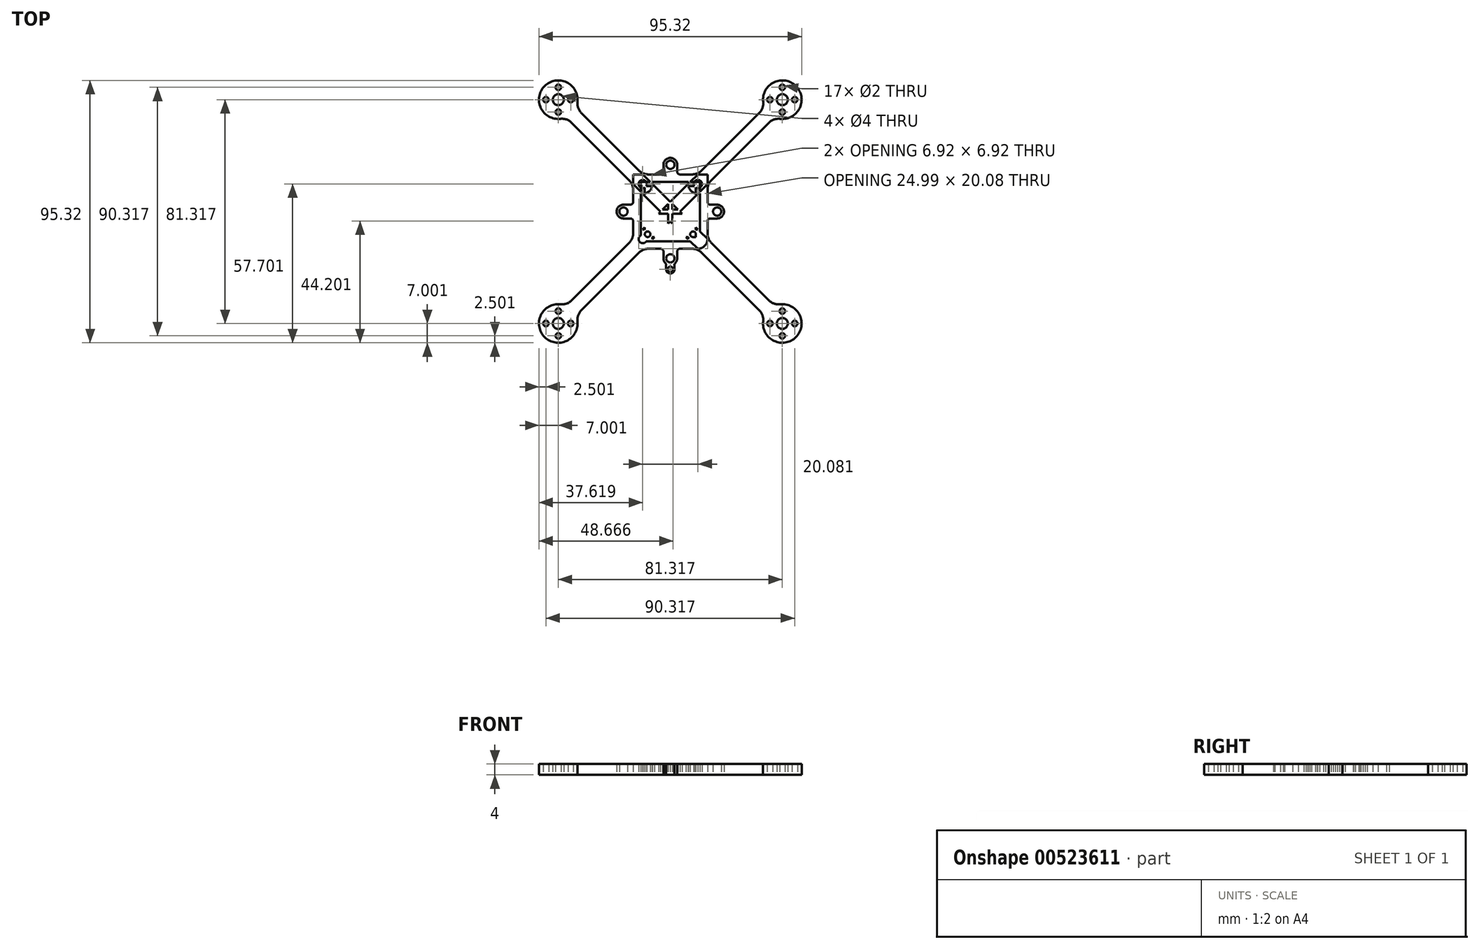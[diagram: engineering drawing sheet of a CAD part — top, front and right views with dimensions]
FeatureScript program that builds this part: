
annotation { "Feature Type Name" : "Feature", "Feature Type Description" : "" }
export const myFeature = defineFeature(function(context is Context, id is Id, definition is map)
    precondition{}
    {
        {
            var Q0;
            Q0=qCreatedBy(makeId("Top.planeOp"),FACE);
            var sketch = newSketch(context, id + "F0", { "sketchPlane" : qUnion([Q0])});
            skLineSegment(sketch, "E0", {"start": v(-40.66, 40.66) * mm, "end": v(40.66, -40.66) * mm});
            skLineSegment(sketch, "E1", {"start": v(40.66, 40.66) * mm, "end": v(-40.66, -40.66) * mm});
            skLineSegment(sketch, "E2.bottom", {"start": v(-13.5, 13.5) * mm, "end": v(13.5, 13.5) * mm});
            skLineSegment(sketch, "E2.top", {"start": v(-13.5, -13.5) * mm, "end": v(13.5, -13.5) * mm});
            skLineSegment(sketch, "E2.left", {"start": v(-13.5, 13.5) * mm, "end": v(-13.5, -13.5) * mm});
            skLineSegment(sketch, "E2.right", {"start": v(13.5, 13.5) * mm, "end": v(13.5, -13.5) * mm});
            skPoint(sketch, "E2.middle", {"position": v(0, 0) * mm});
            skCircle(sketch, "E3", {"center": v(-40.66, 40.66) * mm, "radius": 7 * mm});
            skCircle(sketch, "E4", {"center": v(-40.66, -40.66) * mm, "radius": 7 * mm});
            skCircle(sketch, "E5", {"center": v(40.66, -40.66) * mm, "radius": 7 * mm});
            skCircle(sketch, "E6", {"center": v(40.66, 40.66) * mm, "radius": 7 * mm});
            skPoint(sketch, "E7", {"position": v(-10, 10) * mm});
            skPoint(sketch, "E8", {"position": v(10, 10) * mm});
            skPoint(sketch, "E9", {"position": v(10, -10) * mm});
            skPoint(sketch, "E10", {"position": v(-10, -10) * mm});
            skCircle(sketch, "E11", {"center": v(0, 17) * mm, "radius": 1.5 * mm});
            skCircle(sketch, "E12", {"center": v(-17, 0) * mm, "radius": 1.5 * mm});
            skCircle(sketch, "E13", {"center": v(0, -17) * mm, "radius": 1.5 * mm});
            skCircle(sketch, "E14", {"center": v(0, -21) * mm, "radius": 1 * mm});
            skCircle(sketch, "E15", {"center": v(17, 0) * mm, "radius": 1.5 * mm});
            skCircle(sketch, "E16", {"center": v(0, 17) * mm, "radius": 2.5 * mm});
            skCircle(sketch, "E17", {"center": v(-17, 0) * mm, "radius": 2.5 * mm});
            skCircle(sketch, "E18", {"center": v(0, -17) * mm, "radius": 2.5 * mm});
            skCircle(sketch, "E19", {"center": v(17, 0) * mm, "radius": 2.5 * mm});
            skLineSegment(sketch, "E20", {"start": v(-2.5, 17) * mm, "end": v(-2.5, 13.5) * mm});
            skLineSegment(sketch, "E21", {"start": v(2.5, 17) * mm, "end": v(2.5, 13.5) * mm});
            skLineSegment(sketch, "E22", {"start": v(17, 2.5) * mm, "end": v(13.5, 2.5) * mm});
            skLineSegment(sketch, "E23", {"start": v(17, -2.5) * mm, "end": v(13.5, -2.5) * mm});
            skLineSegment(sketch, "E24", {"start": v(2.5, -17) * mm, "end": v(2.5, -13.5) * mm});
            skLineSegment(sketch, "E25", {"start": v(-2.5, -17) * mm, "end": v(-2.5, -13.5) * mm});
            skLineSegment(sketch, "E26", {"start": v(-17, -2.5) * mm, "end": v(-13.5, -2.5) * mm});
            skLineSegment(sketch, "E27", {"start": v(-17, 2.5) * mm, "end": v(-13.5, 2.5) * mm});
            skCircle(sketch, "E28", {"center": v(0, -21) * mm, "radius": 1.5 * mm});
            skLineSegment(sketch, "E29", {"start": v(-1.5, -21) * mm, "end": v(-1.5, -19) * mm});
            skLineSegment(sketch, "E30", {"start": v(1.5, -21) * mm, "end": v(1.5, -19) * mm});
            skLineSegment(sketch, "E31.0", {"start": v(38.9, 42.43) * mm, "end": v(-42.43, -38.9) * mm});
            skLineSegment(sketch, "E32.0", {"start": v(42.43, 38.9) * mm, "end": v(-38.9, -42.43) * mm});
            skLineSegment(sketch, "E33.0", {"start": v(-42.43, 38.9) * mm, "end": v(38.9, -42.43) * mm});
            skLineSegment(sketch, "E34.0", {"start": v(-38.9, 42.43) * mm, "end": v(42.43, -38.9) * mm});
            skLineSegment(sketch, "E35", {"start": v(-42.43, -38.9) * mm, "end": v(-40.66, -40.66) * mm});
            skLineSegment(sketch, "E36", {"start": v(-38.9, -42.43) * mm, "end": v(-40.66, -40.66) * mm});
            skLineSegment(sketch, "E37", {"start": v(38.9, 42.43) * mm, "end": v(40.66, 40.66) * mm});
            skLineSegment(sketch, "E38", {"start": v(40.66, 40.66) * mm, "end": v(42.43, 38.9) * mm});
            skLineSegment(sketch, "E39", {"start": v(42.43, -38.9) * mm, "end": v(40.66, -40.66) * mm});
            skLineSegment(sketch, "E40", {"start": v(40.66, -40.66) * mm, "end": v(38.9, -42.43) * mm});
            skLineSegment(sketch, "E41", {"start": v(-38.9, 42.43) * mm, "end": v(-40.66, 40.66) * mm});
            skLineSegment(sketch, "E42", {"start": v(-40.66, 40.66) * mm, "end": v(-42.43, 38.9) * mm});
            skPoint(sketch, "E43", {"position": v(-40.66, 45.16) * mm});
            skPoint(sketch, "E44.1.0", {"position": v(-45.16, 40.66) * mm});
            skPoint(sketch, "E44.2.0", {"position": v(-40.66, 36.16) * mm});
            skPoint(sketch, "E45.0.3.0", {"position": v(-36.16, 40.66) * mm});
            skPoint(sketch, "E46", {"position": v(40.66, 45.16) * mm});
            skPoint(sketch, "E47.1.0", {"position": v(36.16, 40.66) * mm});
            skPoint(sketch, "E47.2.0", {"position": v(40.66, 36.16) * mm});
            skLineSegment(sketch, "E47.anchor1", {"start": v(40.66, 40.66) * mm, "end": v(40.66, 45.16) * mm, "construction": true});
            skLineSegment(sketch, "E47.anchor2", {"start": v(40.66, 40.66) * mm, "end": v(45.16, 40.66) * mm, "construction": true});
            skPoint(sketch, "E48.0.3.0", {"position": v(45.16, 40.66) * mm});
            skPoint(sketch, "E49", {"position": v(40.66, -45.16) * mm});
            skPoint(sketch, "E50.1.0", {"position": v(36.16, -40.66) * mm});
            skPoint(sketch, "E50.2.0", {"position": v(40.66, -36.16) * mm});
            skPoint(sketch, "E50.3.0", {"position": v(45.16, -40.66) * mm});
            skLineSegment(sketch, "E50.anchor1", {"start": v(40.66, -40.66) * mm, "end": v(40.66, -45.16) * mm, "construction": true});
            skLineSegment(sketch, "E50.anchor2", {"start": v(40.66, -40.66) * mm, "end": v(45.16, -40.66) * mm, "construction": true});
            skPoint(sketch, "E51", {"position": v(-40.66, -45.16) * mm});
            skPoint(sketch, "E52.1.0", {"position": v(-45.16, -40.66) * mm});
            skPoint(sketch, "E52.2.0", {"position": v(-40.66, -36.16) * mm});
            skPoint(sketch, "E52.3.0", {"position": v(-36.16, -40.66) * mm});
            skLineSegment(sketch, "E52.anchor1", {"start": v(-40.66, -40.66) * mm, "end": v(-40.66, -45.16) * mm, "construction": true});
            skLineSegment(sketch, "E52.anchor2", {"start": v(-40.66, -40.66) * mm, "end": v(-36.16, -40.66) * mm, "construction": true});
            skLineSegment(sketch, "E53.bottom", {"start": v(10.75, -10.75) * mm, "end": v(-10.75, -10.75) * mm});
            skLineSegment(sketch, "E53.top", {"start": v(10.75, 10.75) * mm, "end": v(-10.75, 10.75) * mm});
            skLineSegment(sketch, "E53.left", {"start": v(10.75, -10.75) * mm, "end": v(10.75, 10.75) * mm});
            skLineSegment(sketch, "E53.right", {"start": v(-10.75, -10.75) * mm, "end": v(-10.75, 10.75) * mm});
            skLineSegment(sketch, "E54.bottom", {"start": v(-9.25, -9.25) * mm, "end": v(9.25, -9.25) * mm});
            skLineSegment(sketch, "E54.top", {"start": v(-9.25, 9.25) * mm, "end": v(9.25, 9.25) * mm});
            skLineSegment(sketch, "E54.left", {"start": v(-9.25, -9.25) * mm, "end": v(-9.25, 9.25) * mm});
            skLineSegment(sketch, "E54.right", {"start": v(9.25, -9.25) * mm, "end": v(9.25, 9.25) * mm});
            skLineSegment(sketch, "E55.bottom", {"start": v(-0.75, 9.25) * mm, "end": v(0.75, 9.25) * mm});
            skLineSegment(sketch, "E55.top", {"start": v(-0.75, -9.25) * mm, "end": v(0.75, -9.25) * mm});
            skLineSegment(sketch, "E55.left", {"start": v(-0.75, 9.25) * mm, "end": v(-0.75, -9.25) * mm});
            skLineSegment(sketch, "E55.right", {"start": v(0.75, 9.25) * mm, "end": v(0.75, -9.25) * mm});
            skLineSegment(sketch, "E56.bottom", {"start": v(-9.25, -0.75) * mm, "end": v(9.25, -0.75) * mm});
            skLineSegment(sketch, "E56.top", {"start": v(-9.25, 0.75) * mm, "end": v(9.25, 0.75) * mm});
            skLineSegment(sketch, "E56.left", {"start": v(-9.25, -0.75) * mm, "end": v(-9.25, 0.75) * mm});
            skLineSegment(sketch, "E56.right", {"start": v(9.25, -0.75) * mm, "end": v(9.25, 0.75) * mm});
            skPoint(sketch, "E56.cornerSnap0", {"position": v(-1.77, -0.75) * mm});
            skCircle(sketch, "E57", {"center": v(-40.66, 40.66) * mm, "radius": 2 * mm});
            skCircle(sketch, "E58", {"center": v(40.66, 40.66) * mm, "radius": 2 * mm});
            skCircle(sketch, "E59", {"center": v(40.66, -40.66) * mm, "radius": 2 * mm});
            skCircle(sketch, "E60", {"center": v(-40.66, -40.66) * mm, "radius": 2 * mm});
            skCircle(sketch, "E61", {"center": v(-40.66, 45.16) * mm, "radius": 1 * mm});
            skCircle(sketch, "E62", {"center": v(-45.16, 40.66) * mm, "radius": 1 * mm});
            skCircle(sketch, "E63", {"center": v(-36.16, 40.66) * mm, "radius": 1 * mm});
            skCircle(sketch, "E64", {"center": v(-40.66, 36.16) * mm, "radius": 1 * mm});
            skCircle(sketch, "E65", {"center": v(45.16, 40.66) * mm, "radius": 1 * mm});
            skCircle(sketch, "E66", {"center": v(40.66, 45.16) * mm, "radius": 1 * mm});
            skCircle(sketch, "E67", {"center": v(40.66, 36.16) * mm, "radius": 1 * mm});
            skCircle(sketch, "E68", {"center": v(36.16, 40.66) * mm, "radius": 1 * mm});
            skCircle(sketch, "E69", {"center": v(45.16, -40.66) * mm, "radius": 1 * mm});
            skCircle(sketch, "E70", {"center": v(40.66, -36.16) * mm, "radius": 1 * mm});
            skCircle(sketch, "E71", {"center": v(40.66, -45.16) * mm, "radius": 1 * mm});
            skCircle(sketch, "E72", {"center": v(36.16, -40.66) * mm, "radius": 1 * mm});
            skCircle(sketch, "E73", {"center": v(-36.16, -40.66) * mm, "radius": 1 * mm});
            skCircle(sketch, "E74", {"center": v(-40.66, -45.16) * mm, "radius": 1 * mm});
            skCircle(sketch, "E75", {"center": v(-45.16, -40.66) * mm, "radius": 1 * mm});
            skCircle(sketch, "E76", {"center": v(-40.66, -36.16) * mm, "radius": 1 * mm});
            skCircle(sketch, "E77", {"center": v(-10, 10) * mm, "radius": 1.5 * mm});
            skCircle(sketch, "E78", {"center": v(-10, -10) * mm, "radius": 3.5 * mm});
            skCircle(sketch, "E79", {"center": v(10, -10) * mm, "radius": 3.5 * mm});
            skCircle(sketch, "E80", {"center": v(10, 10) * mm, "radius": 3.5 * mm});
            skCircle(sketch, "E81", {"center": v(-10, 10) * mm, "radius": 3.5 * mm});
            skCircle(sketch, "E82", {"center": v(-10, -10) * mm, "radius": 1.5 * mm});
            skCircle(sketch, "E83", {"center": v(10, -10) * mm, "radius": 1.5 * mm});
            skCircle(sketch, "E84", {"center": v(10, 10) * mm, "radius": 1.5 * mm});
            skSolve(sketch);
        }
        {
            var Q0;
            {var subQ0=sQuery(id+"F0.wireOp",EDGE,"E55.bottom");Q0=makeQuery(id+"F0.imprint","IMPRINT",FACE,{"disambiguationData":[TD([[makeQuery(id+"F0.imprint","IMPRINT",EDGE,{"derivedFrom":subQ0}),1.0]])]});}
            var Q1;
            {var subQ0=sQuery(id+"F0.wireOp",EDGE,"E56.left");Q1=makeQuery(id+"F0.imprint","IMPRINT",FACE,{"disambiguationData":[TD([[makeQuery(id+"F0.imprint","IMPRINT",EDGE,{"derivedFrom":subQ0}),1.0]])]});}
            var Q2;
            {var subQ3=sQuery(id+"F0.wireOp",EDGE,"E54.left");var subQ5=sQuery(id+"F0.wireOp",EDGE,"E31.0");var subQ7=makeQuery(id+"F0.imprint","INTERSECT",VERTEX,{"derivedFrom":[subQ5,subQ3]});Q2=makeQuery(id+"F0.imprint","IMPRINT",FACE,{"disambiguationData":[TD([[makeQuery(id+"F0.imprint","IMPRINT",EDGE,{"disambiguationData":[TD([[subQ7,-1.0]])],"derivedFrom":subQ5}),1.0]])]});}
            var Q3;
            {var subQ7=sQuery(id+"F0.wireOp",EDGE,"E55.top");Q3=makeQuery(id+"F0.imprint","IMPRINT",FACE,{"disambiguationData":[TD([[makeQuery(id+"F0.imprint","IMPRINT",EDGE,{"derivedFrom":subQ7}),-1.0]])]});}
            var Q4;
            {var subQ3=sQuery(id+"F0.wireOp",EDGE,"E54.bottom");var subQ5=sQuery(id+"F0.wireOp",EDGE,"E32.0");var subQ6=makeQuery(id+"F0.imprint","INTERSECT",VERTEX,{"derivedFrom":[subQ5,subQ3]});Q4=makeQuery(id+"F0.imprint","IMPRINT",FACE,{"disambiguationData":[TD([[makeQuery(id+"F0.imprint","IMPRINT",EDGE,{"disambiguationData":[TD([[subQ6,-1.0]])],"derivedFrom":subQ5}),-1.0]])]});}
            var Q5;
            {var subQ3=sQuery(id+"F0.wireOp",EDGE,"E54.bottom");var subQ5=sQuery(id+"F0.wireOp",EDGE,"E33.0");var subQ6=makeQuery(id+"F0.imprint","INTERSECT",VERTEX,{"derivedFrom":[subQ5,subQ3]});Q5=makeQuery(id+"F0.imprint","IMPRINT",FACE,{"disambiguationData":[TD([[makeQuery(id+"F0.imprint","IMPRINT",EDGE,{"disambiguationData":[TD([[subQ6,-1.0]])],"derivedFrom":subQ5}),1.0]])]});}
            var Q6;
            {var subQ5=sQuery(id+"F0.wireOp",EDGE,"E56.right");Q6=makeQuery(id+"F0.imprint","IMPRINT",FACE,{"disambiguationData":[TD([[makeQuery(id+"F0.imprint","IMPRINT",EDGE,{"derivedFrom":subQ5}),-1.0]])]});}
            var Q7;
            {var subQ3=sQuery(id+"F0.wireOp",EDGE,"E54.right");var subQ5=sQuery(id+"F0.wireOp",EDGE,"E34.0");var subQ6=makeQuery(id+"F0.imprint","INTERSECT",VERTEX,{"derivedFrom":[subQ5,subQ3]});Q7=makeQuery(id+"F0.imprint","IMPRINT",FACE,{"disambiguationData":[TD([[makeQuery(id+"F0.imprint","IMPRINT",EDGE,{"disambiguationData":[TD([[subQ6,-1.0]])],"derivedFrom":subQ5}),-1.0]])]});}
            var Q8;
            {var subQ0=sQuery(id+"F0.wireOp",EDGE,"E55.bottom");Q8=makeQuery(id+"F0.imprint","IMPRINT",FACE,{"disambiguationData":[TD([[makeQuery(id+"F0.imprint","IMPRINT",EDGE,{"derivedFrom":subQ0}),-1.0]])]});}
            var Q9;
            {var subQ1=sQuery(id+"F0.wireOp",EDGE,"E31.0");var subQ7=sQuery(id+"F0.wireOp",EDGE,"E34.0");var subQ9=makeQuery(id+"F0.imprint","INTERSECT",VERTEX,{"derivedFrom":[subQ1,subQ7]});Q9=makeQuery(id+"F0.imprint","IMPRINT",FACE,{"disambiguationData":[TD([[makeQuery(id+"F0.imprint","IMPRINT",EDGE,{"disambiguationData":[TD([[subQ9,-1.0]])],"derivedFrom":subQ1}),1.0]])]});}
            var Q10;
            {var subQ0=sQuery(id+"F0.wireOp",EDGE,"E55.right");var subQ1=sQuery(id+"F0.wireOp",EDGE,"E31.0");var subQ2=makeQuery(id+"F0.imprint","INTERSECT",VERTEX,{"derivedFrom":[subQ1,subQ0]});Q10=makeQuery(id+"F0.imprint","IMPRINT",FACE,{"disambiguationData":[TD([[makeQuery(id+"F0.imprint","IMPRINT",EDGE,{"disambiguationData":[TD([[subQ2,-1.0]])],"derivedFrom":subQ1}),1.0]])]});}
            var Q11;
            {var subQ0=sQuery(id+"F0.wireOp",EDGE,"E34.0");var subQ1=sQuery(id+"F0.wireOp",EDGE,"E31.0");var subQ2=makeQuery(id+"F0.imprint","INTERSECT",VERTEX,{"derivedFrom":[subQ1,subQ0]});Q11=makeQuery(id+"F0.imprint","IMPRINT",FACE,{"disambiguationData":[TD([[makeQuery(id+"F0.imprint","IMPRINT",EDGE,{"disambiguationData":[TD([[subQ2,-1.0]])],"derivedFrom":subQ1}),-1.0]])]});}
            var Q12;
            {var subQ0=sQuery(id+"F0.wireOp",EDGE,"E1");var subQ1=sQuery(id+"F0.wireOp",EDGE,"E0");var subQ2=makeQuery(id+"F0.imprint","INTERSECT",VERTEX,{"derivedFrom":[subQ1,subQ0]});Q12=makeQuery(id+"F0.imprint","IMPRINT",FACE,{"disambiguationData":[TD([[makeQuery(id+"F0.imprint","IMPRINT",EDGE,{"disambiguationData":[TD([[subQ2,1.0]])],"derivedFrom":subQ1}),1.0]])]});}
            var Q13;
            {var subQ0=sQuery(id+"F0.wireOp",EDGE,"E1");var subQ1=sQuery(id+"F0.wireOp",EDGE,"E0");var subQ2=makeQuery(id+"F0.imprint","INTERSECT",VERTEX,{"derivedFrom":[subQ1,subQ0]});Q13=makeQuery(id+"F0.imprint","IMPRINT",FACE,{"disambiguationData":[TD([[makeQuery(id+"F0.imprint","IMPRINT",EDGE,{"disambiguationData":[TD([[subQ2,1.0]])],"derivedFrom":subQ1}),-1.0]])]});}
            var Q14;
            {var subQ0=sQuery(id+"F0.wireOp",EDGE,"E1");var subQ1=sQuery(id+"F0.wireOp",EDGE,"E0");var subQ2=makeQuery(id+"F0.imprint","INTERSECT",VERTEX,{"derivedFrom":[subQ1,subQ0]});Q14=makeQuery(id+"F0.imprint","IMPRINT",FACE,{"disambiguationData":[TD([[makeQuery(id+"F0.imprint","IMPRINT",EDGE,{"disambiguationData":[TD([[subQ2,-1.0]])],"derivedFrom":subQ1}),-1.0]])]});}
            var Q15;
            {var subQ0=sQuery(id+"F0.wireOp",EDGE,"E1");var subQ1=sQuery(id+"F0.wireOp",EDGE,"E0");var subQ2=makeQuery(id+"F0.imprint","INTERSECT",VERTEX,{"derivedFrom":[subQ1,subQ0]});Q15=makeQuery(id+"F0.imprint","IMPRINT",FACE,{"disambiguationData":[TD([[makeQuery(id+"F0.imprint","IMPRINT",EDGE,{"disambiguationData":[TD([[subQ2,-1.0]])],"derivedFrom":subQ1}),1.0]])]});}
            var Q16;
            {var subQ1=sQuery(id+"F0.wireOp",EDGE,"E32.0");var subQ7=sQuery(id+"F0.wireOp",EDGE,"E34.0");var subQ8=makeQuery(id+"F0.imprint","INTERSECT",VERTEX,{"derivedFrom":[subQ1,subQ7]});Q16=makeQuery(id+"F0.imprint","IMPRINT",FACE,{"disambiguationData":[TD([[makeQuery(id+"F0.imprint","IMPRINT",EDGE,{"disambiguationData":[TD([[subQ8,-1.0]])],"derivedFrom":subQ1}),-1.0]])]});}
            var Q17;
            {var subQ0=sQuery(id+"F0.wireOp",EDGE,"E56.top");var subQ1=sQuery(id+"F0.wireOp",EDGE,"E32.0");var subQ2=makeQuery(id+"F0.imprint","INTERSECT",VERTEX,{"derivedFrom":[subQ1,subQ0]});Q17=makeQuery(id+"F0.imprint","IMPRINT",FACE,{"disambiguationData":[TD([[makeQuery(id+"F0.imprint","IMPRINT",EDGE,{"disambiguationData":[TD([[subQ2,-1.0]])],"derivedFrom":subQ1}),-1.0]])]});}
            var Q18;
            {var subQ0=sQuery(id+"F0.wireOp",EDGE,"E34.0");var subQ1=sQuery(id+"F0.wireOp",EDGE,"E32.0");var subQ2=makeQuery(id+"F0.imprint","INTERSECT",VERTEX,{"derivedFrom":[subQ1,subQ0]});Q18=makeQuery(id+"F0.imprint","IMPRINT",FACE,{"disambiguationData":[TD([[makeQuery(id+"F0.imprint","IMPRINT",EDGE,{"disambiguationData":[TD([[subQ2,-1.0]])],"derivedFrom":subQ1}),1.0]])]});}
            var Q19;
            {var subQ0=sQuery(id+"F0.wireOp",EDGE,"E56.right");Q19=makeQuery(id+"F0.imprint","IMPRINT",FACE,{"disambiguationData":[TD([[makeQuery(id+"F0.imprint","IMPRINT",EDGE,{"derivedFrom":subQ0}),1.0]])]});}
            var Q20;
            {var subQ5=sQuery(id+"F0.wireOp",EDGE,"E55.right");var subQ6=sQuery(id+"F0.wireOp",EDGE,"E32.0");var subQ7=makeQuery(id+"F0.imprint","INTERSECT",VERTEX,{"derivedFrom":[subQ6,subQ5]});Q20=makeQuery(id+"F0.imprint","IMPRINT",FACE,{"disambiguationData":[TD([[makeQuery(id+"F0.imprint","IMPRINT",EDGE,{"disambiguationData":[TD([[subQ7,-1.0]])],"derivedFrom":subQ6}),-1.0]])]});}
            var Q21;
            {var subQ0=sQuery(id+"F0.wireOp",EDGE,"E33.0");var subQ1=sQuery(id+"F0.wireOp",EDGE,"E32.0");var subQ2=makeQuery(id+"F0.imprint","INTERSECT",VERTEX,{"derivedFrom":[subQ1,subQ0]});Q21=makeQuery(id+"F0.imprint","IMPRINT",FACE,{"disambiguationData":[TD([[makeQuery(id+"F0.imprint","IMPRINT",EDGE,{"disambiguationData":[TD([[subQ2,-1.0]])],"derivedFrom":subQ1}),-1.0]])]});}
            var Q22;
            {var subQ0=sQuery(id+"F0.wireOp",EDGE,"E55.right");var subQ1=sQuery(id+"F0.wireOp",EDGE,"E32.0");var subQ2=makeQuery(id+"F0.imprint","INTERSECT",VERTEX,{"derivedFrom":[subQ1,subQ0]});Q22=makeQuery(id+"F0.imprint","IMPRINT",FACE,{"disambiguationData":[TD([[makeQuery(id+"F0.imprint","IMPRINT",EDGE,{"disambiguationData":[TD([[subQ2,-1.0]])],"derivedFrom":subQ1}),1.0]])]});}
            var Q23;
            {var subQ0=sQuery(id+"F0.wireOp",EDGE,"E55.top");Q23=makeQuery(id+"F0.imprint","IMPRINT",FACE,{"disambiguationData":[TD([[makeQuery(id+"F0.imprint","IMPRINT",EDGE,{"derivedFrom":subQ0}),1.0]])]});}
            var Q24;
            {var subQ5=sQuery(id+"F0.wireOp",EDGE,"E31.0");var subQ7=sQuery(id+"F0.wireOp",EDGE,"E56.top");var subQ9=makeQuery(id+"F0.imprint","INTERSECT",VERTEX,{"derivedFrom":[subQ5,subQ7]});Q24=makeQuery(id+"F0.imprint","IMPRINT",FACE,{"disambiguationData":[TD([[makeQuery(id+"F0.imprint","IMPRINT",EDGE,{"disambiguationData":[TD([[subQ9,-1.0]])],"derivedFrom":subQ5}),1.0]])]});}
            var Q25;
            {var subQ0=sQuery(id+"F0.wireOp",EDGE,"E56.top");var subQ1=sQuery(id+"F0.wireOp",EDGE,"E31.0");var subQ2=makeQuery(id+"F0.imprint","INTERSECT",VERTEX,{"derivedFrom":[subQ1,subQ0]});Q25=makeQuery(id+"F0.imprint","IMPRINT",FACE,{"disambiguationData":[TD([[makeQuery(id+"F0.imprint","IMPRINT",EDGE,{"disambiguationData":[TD([[subQ2,-1.0]])],"derivedFrom":subQ1}),-1.0]])]});}
            var Q26;
            {var subQ0=sQuery(id+"F0.wireOp",EDGE,"E33.0");var subQ1=sQuery(id+"F0.wireOp",EDGE,"E31.0");var subQ2=makeQuery(id+"F0.imprint","INTERSECT",VERTEX,{"derivedFrom":[subQ1,subQ0]});Q26=makeQuery(id+"F0.imprint","IMPRINT",FACE,{"disambiguationData":[TD([[makeQuery(id+"F0.imprint","IMPRINT",EDGE,{"disambiguationData":[TD([[subQ2,-1.0]])],"derivedFrom":subQ1}),1.0]])]});}
            var Q27;
            {var subQ0=sQuery(id+"F0.wireOp",EDGE,"E56.left");Q27=makeQuery(id+"F0.imprint","IMPRINT",FACE,{"disambiguationData":[TD([[makeQuery(id+"F0.imprint","IMPRINT",EDGE,{"derivedFrom":subQ0}),-1.0]])]});}
            var Q28;
            {var subQ1=sQuery(id+"F0.wireOp",EDGE,"E1");var subQ3=sQuery(id+"F0.wireOp",EDGE,"E78");var subQ4=makeQuery(id+"F0.imprint","INTERSECT",VERTEX,{"disambiguationData":[OD(1.0)],"derivedFrom":[subQ1,subQ3]});Q28=makeQuery(id+"F0.imprint","IMPRINT",FACE,{"disambiguationData":[TD([[makeQuery(id+"F0.imprint","IMPRINT",EDGE,{"disambiguationData":[TD([[subQ4,1.0]])],"derivedFrom":subQ3}),-1.0]])]});}
            var Q29;
            {var subQ1=sQuery(id+"F0.wireOp",EDGE,"E1");var subQ3=sQuery(id+"F0.wireOp",EDGE,"E78");var subQ4=makeQuery(id+"F0.imprint","INTERSECT",VERTEX,{"disambiguationData":[OD(1.0)],"derivedFrom":[subQ1,subQ3]});Q29=makeQuery(id+"F0.imprint","IMPRINT",FACE,{"disambiguationData":[TD([[makeQuery(id+"F0.imprint","IMPRINT",EDGE,{"disambiguationData":[TD([[subQ4,-1.0]])],"derivedFrom":subQ3}),-1.0]])]});}
            var Q30;
            {var subQ3=sQuery(id+"F0.wireOp",EDGE,"E82");var subQ8=sQuery(id+"F0.wireOp",EDGE,"E1");var subQ9=makeQuery(id+"F0.imprint","INTERSECT",VERTEX,{"disambiguationData":[OD(1.0)],"derivedFrom":[subQ8,subQ3]});Q30=makeQuery(id+"F0.imprint","IMPRINT",FACE,{"disambiguationData":[TD([[makeQuery(id+"F0.imprint","IMPRINT",EDGE,{"disambiguationData":[TD([[subQ9,-1.0]])],"derivedFrom":subQ8}),-1.0]])]});}
            var Q31;
            {var subQ1=sQuery(id+"F0.wireOp",EDGE,"E1");var subQ7=sQuery(id+"F0.wireOp",EDGE,"E82");var subQ10=makeQuery(id+"F0.imprint","INTERSECT",VERTEX,{"disambiguationData":[OD(1.0)],"derivedFrom":[subQ1,subQ7]});Q31=makeQuery(id+"F0.imprint","IMPRINT",FACE,{"disambiguationData":[TD([[makeQuery(id+"F0.imprint","IMPRINT",EDGE,{"disambiguationData":[TD([[subQ10,-1.0]])],"derivedFrom":subQ1}),1.0]])]});}
            var Q32;
            {var subQ0=sQuery(id+"F0.wireOp",EDGE,"E53.right");var subQ1=sQuery(id+"F0.wireOp",EDGE,"E31.0");var subQ2=makeQuery(id+"F0.imprint","INTERSECT",VERTEX,{"derivedFrom":[subQ1,subQ0]});Q32=makeQuery(id+"F0.imprint","IMPRINT",FACE,{"disambiguationData":[TD([[makeQuery(id+"F0.imprint","IMPRINT",EDGE,{"disambiguationData":[TD([[subQ2,-1.0]])],"derivedFrom":subQ1}),-1.0]])]});}
            var Q33;
            {var subQ0=sQuery(id+"F0.wireOp",EDGE,"E78");var subQ1=sQuery(id+"F0.wireOp",EDGE,"E32.0");var subQ2=makeQuery(id+"F0.imprint","INTERSECT",VERTEX,{"disambiguationData":[OD(0.0)],"derivedFrom":[subQ1,subQ0]});Q33=makeQuery(id+"F0.imprint","IMPRINT",FACE,{"disambiguationData":[TD([[makeQuery(id+"F0.imprint","IMPRINT",EDGE,{"disambiguationData":[TD([[subQ2,-1.0]])],"derivedFrom":subQ1}),-1.0]])]});}
            var Q34;
            {var subQ0=sQuery(id+"F0.wireOp",EDGE,"E78");var subQ1=sQuery(id+"F0.wireOp",EDGE,"E1");var subQ2=makeQuery(id+"F0.imprint","INTERSECT",VERTEX,{"disambiguationData":[OD(0.0)],"derivedFrom":[subQ1,subQ0]});Q34=makeQuery(id+"F0.imprint","IMPRINT",FACE,{"disambiguationData":[TD([[makeQuery(id+"F0.imprint","IMPRINT",EDGE,{"disambiguationData":[TD([[subQ2,-1.0]])],"derivedFrom":subQ1}),-1.0]])]});}
            var Q35;
            {var subQ0=sQuery(id+"F0.wireOp",EDGE,"E78");var subQ1=sQuery(id+"F0.wireOp",EDGE,"E31.0");var subQ2=makeQuery(id+"F0.imprint","INTERSECT",VERTEX,{"disambiguationData":[OD(0.0)],"derivedFrom":[subQ1,subQ0]});Q35=makeQuery(id+"F0.imprint","IMPRINT",FACE,{"disambiguationData":[TD([[makeQuery(id+"F0.imprint","IMPRINT",EDGE,{"disambiguationData":[TD([[subQ2,-1.0]])],"derivedFrom":subQ1}),1.0]])]});}
            var Q36;
            {var subQ0=sQuery(id+"F0.wireOp",EDGE,"E78");var subQ1=sQuery(id+"F0.wireOp",EDGE,"E1");var subQ2=makeQuery(id+"F0.imprint","INTERSECT",VERTEX,{"disambiguationData":[OD(0.0)],"derivedFrom":[subQ1,subQ0]});Q36=makeQuery(id+"F0.imprint","IMPRINT",FACE,{"disambiguationData":[TD([[makeQuery(id+"F0.imprint","IMPRINT",EDGE,{"disambiguationData":[TD([[subQ2,-1.0]])],"derivedFrom":subQ1}),1.0]])]});}
            var Q37;
            {var subQ0=sQuery(id+"F0.wireOp",EDGE,"E53.bottom");var subQ1=sQuery(id+"F0.wireOp",EDGE,"E32.0");var subQ2=makeQuery(id+"F0.imprint","INTERSECT",VERTEX,{"derivedFrom":[subQ1,subQ0]});Q37=makeQuery(id+"F0.imprint","IMPRINT",FACE,{"disambiguationData":[TD([[makeQuery(id+"F0.imprint","IMPRINT",EDGE,{"disambiguationData":[TD([[subQ2,-1.0]])],"derivedFrom":subQ1}),1.0]])]});}
            var Q38;
            {var subQ0=sQuery(id+"F0.wireOp",EDGE,"E78");var subQ1=sQuery(id+"F0.wireOp",EDGE,"E32.0");var subQ2=makeQuery(id+"F0.imprint","INTERSECT",VERTEX,{"disambiguationData":[OD(0.0)],"derivedFrom":[subQ1,subQ0]});Q38=makeQuery(id+"F0.imprint","IMPRINT",FACE,{"disambiguationData":[TD([[makeQuery(id+"F0.imprint","IMPRINT",EDGE,{"disambiguationData":[TD([[subQ2,-1.0]])],"derivedFrom":subQ1}),1.0]])]});}
            var Q39;
            {var subQ0=sQuery(id+"F0.wireOp",EDGE,"E78");var subQ1=sQuery(id+"F0.wireOp",EDGE,"E31.0");var subQ2=makeQuery(id+"F0.imprint","INTERSECT",VERTEX,{"disambiguationData":[OD(0.0)],"derivedFrom":[subQ1,subQ0]});Q39=makeQuery(id+"F0.imprint","IMPRINT",FACE,{"disambiguationData":[TD([[makeQuery(id+"F0.imprint","IMPRINT",EDGE,{"disambiguationData":[TD([[subQ2,-1.0]])],"derivedFrom":subQ1}),-1.0]])]});}
            var Q40;
            {var subQ1=sQuery(id+"F0.wireOp",EDGE,"E0");var subQ3=sQuery(id+"F0.wireOp",EDGE,"E81");var subQ4=makeQuery(id+"F0.imprint","INTERSECT",VERTEX,{"disambiguationData":[OD(0.0)],"derivedFrom":[subQ1,subQ3]});Q40=makeQuery(id+"F0.imprint","IMPRINT",FACE,{"disambiguationData":[TD([[makeQuery(id+"F0.imprint","IMPRINT",EDGE,{"disambiguationData":[TD([[subQ4,-1.0]])],"derivedFrom":subQ3}),-1.0]])]});}
            var Q41;
            {var subQ0=sQuery(id+"F0.wireOp",EDGE,"E81");var subQ1=sQuery(id+"F0.wireOp",EDGE,"E34.0");var subQ2=makeQuery(id+"F0.imprint","INTERSECT",VERTEX,{"disambiguationData":[OD(0.0)],"derivedFrom":[subQ1,subQ0]});Q41=makeQuery(id+"F0.imprint","IMPRINT",FACE,{"disambiguationData":[TD([[makeQuery(id+"F0.imprint","IMPRINT",EDGE,{"disambiguationData":[TD([[subQ2,-1.0]])],"derivedFrom":subQ1}),1.0]])]});}
            var Q42;
            {var subQ1=sQuery(id+"F0.wireOp",EDGE,"E0");var subQ3=sQuery(id+"F0.wireOp",EDGE,"E81");var subQ4=makeQuery(id+"F0.imprint","INTERSECT",VERTEX,{"disambiguationData":[OD(0.0)],"derivedFrom":[subQ1,subQ3]});Q42=makeQuery(id+"F0.imprint","IMPRINT",FACE,{"disambiguationData":[TD([[makeQuery(id+"F0.imprint","IMPRINT",EDGE,{"disambiguationData":[TD([[subQ4,1.0]])],"derivedFrom":subQ3}),-1.0]])]});}
            var Q43;
            {var subQ1=sQuery(id+"F0.wireOp",EDGE,"E0");var subQ7=sQuery(id+"F0.wireOp",EDGE,"E81");var subQ9=makeQuery(id+"F0.imprint","INTERSECT",VERTEX,{"disambiguationData":[OD(0.0)],"derivedFrom":[subQ1,subQ7]});Q43=makeQuery(id+"F0.imprint","IMPRINT",FACE,{"disambiguationData":[TD([[makeQuery(id+"F0.imprint","IMPRINT",EDGE,{"disambiguationData":[TD([[subQ9,-1.0]])],"derivedFrom":subQ1}),-1.0]])]});}
            var Q44;
            {var subQ0=sQuery(id+"F0.wireOp",EDGE,"E81");var subQ1=sQuery(id+"F0.wireOp",EDGE,"E33.0");var subQ2=makeQuery(id+"F0.imprint","INTERSECT",VERTEX,{"disambiguationData":[OD(0.0)],"derivedFrom":[subQ1,subQ0]});Q44=makeQuery(id+"F0.imprint","IMPRINT",FACE,{"disambiguationData":[TD([[makeQuery(id+"F0.imprint","IMPRINT",EDGE,{"disambiguationData":[TD([[subQ2,-1.0]])],"derivedFrom":subQ1}),-1.0]])]});}
            var Q45;
            {var subQ0=sQuery(id+"F0.wireOp",EDGE,"E53.right");var subQ1=sQuery(id+"F0.wireOp",EDGE,"E33.0");var subQ2=makeQuery(id+"F0.imprint","INTERSECT",VERTEX,{"derivedFrom":[subQ1,subQ0]});Q45=makeQuery(id+"F0.imprint","IMPRINT",FACE,{"disambiguationData":[TD([[makeQuery(id+"F0.imprint","IMPRINT",EDGE,{"disambiguationData":[TD([[subQ2,-1.0]])],"derivedFrom":subQ1}),-1.0]])]});}
            var Q46;
            {var subQ1=sQuery(id+"F0.wireOp",EDGE,"E53.right");var subQ7=sQuery(id+"F0.wireOp",EDGE,"E33.0");var subQ8=makeQuery(id+"F0.imprint","INTERSECT",VERTEX,{"derivedFrom":[subQ7,subQ1]});Q46=makeQuery(id+"F0.imprint","IMPRINT",FACE,{"disambiguationData":[TD([[makeQuery(id+"F0.imprint","IMPRINT",EDGE,{"disambiguationData":[TD([[subQ8,-1.0]])],"derivedFrom":subQ7}),1.0]])]});}
            var Q47;
            {var subQ0=sQuery(id+"F0.wireOp",EDGE,"E77");var subQ1=sQuery(id+"F0.wireOp",EDGE,"E0");var subQ2=makeQuery(id+"F0.imprint","INTERSECT",VERTEX,{"disambiguationData":[OD(1.0)],"derivedFrom":[subQ1,subQ0]});Q47=makeQuery(id+"F0.imprint","IMPRINT",FACE,{"disambiguationData":[TD([[makeQuery(id+"F0.imprint","IMPRINT",EDGE,{"disambiguationData":[TD([[subQ2,-1.0]])],"derivedFrom":subQ1}),-1.0]])]});}
            var Q48;
            {var subQ0=sQuery(id+"F0.wireOp",EDGE,"E77");var subQ1=sQuery(id+"F0.wireOp",EDGE,"E0");var subQ2=makeQuery(id+"F0.imprint","INTERSECT",VERTEX,{"disambiguationData":[OD(1.0)],"derivedFrom":[subQ1,subQ0]});Q48=makeQuery(id+"F0.imprint","IMPRINT",FACE,{"disambiguationData":[TD([[makeQuery(id+"F0.imprint","IMPRINT",EDGE,{"disambiguationData":[TD([[subQ2,-1.0]])],"derivedFrom":subQ1}),1.0]])]});}
            var Q49;
            {var subQ1=sQuery(id+"F0.wireOp",EDGE,"E0");var subQ5=sQuery(id+"F0.wireOp",EDGE,"E81");var subQ10=makeQuery(id+"F0.imprint","INTERSECT",VERTEX,{"disambiguationData":[OD(0.0)],"derivedFrom":[subQ1,subQ5]});Q49=makeQuery(id+"F0.imprint","IMPRINT",FACE,{"disambiguationData":[TD([[makeQuery(id+"F0.imprint","IMPRINT",EDGE,{"disambiguationData":[TD([[subQ10,-1.0]])],"derivedFrom":subQ1}),1.0]])]});}
            var Q50;
            {var subQ0=sQuery(id+"F0.wireOp",EDGE,"E81");var subQ1=sQuery(id+"F0.wireOp",EDGE,"E33.0");var subQ2=makeQuery(id+"F0.imprint","INTERSECT",VERTEX,{"disambiguationData":[OD(1.0)],"derivedFrom":[subQ1,subQ0]});Q50=makeQuery(id+"F0.imprint","IMPRINT",FACE,{"disambiguationData":[TD([[makeQuery(id+"F0.imprint","IMPRINT",EDGE,{"disambiguationData":[TD([[subQ2,-1.0]])],"derivedFrom":subQ1}),1.0]])]});}
            var Q51;
            {var subQ0=sQuery(id+"F0.wireOp",EDGE,"E81");var subQ1=sQuery(id+"F0.wireOp",EDGE,"E34.0");var subQ2=makeQuery(id+"F0.imprint","INTERSECT",VERTEX,{"disambiguationData":[OD(1.0)],"derivedFrom":[subQ1,subQ0]});Q51=makeQuery(id+"F0.imprint","IMPRINT",FACE,{"disambiguationData":[TD([[makeQuery(id+"F0.imprint","IMPRINT",EDGE,{"disambiguationData":[TD([[subQ2,-1.0]])],"derivedFrom":subQ1}),-1.0]])]});}
            var Q52;
            {var subQ0=sQuery(id+"F0.wireOp",EDGE,"E53.top");var subQ1=sQuery(id+"F0.wireOp",EDGE,"E34.0");var subQ2=makeQuery(id+"F0.imprint","INTERSECT",VERTEX,{"derivedFrom":[subQ1,subQ0]});Q52=makeQuery(id+"F0.imprint","IMPRINT",FACE,{"disambiguationData":[TD([[makeQuery(id+"F0.imprint","IMPRINT",EDGE,{"disambiguationData":[TD([[subQ2,-1.0]])],"derivedFrom":subQ1}),1.0]])]});}
            var Q53;
            {var subQ1=sQuery(id+"F0.wireOp",EDGE,"E53.top");var subQ5=sQuery(id+"F0.wireOp",EDGE,"E34.0");var subQ6=makeQuery(id+"F0.imprint","INTERSECT",VERTEX,{"derivedFrom":[subQ5,subQ1]});Q53=makeQuery(id+"F0.imprint","IMPRINT",FACE,{"disambiguationData":[TD([[makeQuery(id+"F0.imprint","IMPRINT",EDGE,{"disambiguationData":[TD([[subQ6,-1.0]])],"derivedFrom":subQ5}),-1.0]])]});}
            var Q54;
            {var subQ1=sQuery(id+"F0.wireOp",EDGE,"E1");var subQ3=sQuery(id+"F0.wireOp",EDGE,"E80");var subQ4=makeQuery(id+"F0.imprint","INTERSECT",VERTEX,{"disambiguationData":[OD(0.0)],"derivedFrom":[subQ1,subQ3]});Q54=makeQuery(id+"F0.imprint","IMPRINT",FACE,{"disambiguationData":[TD([[makeQuery(id+"F0.imprint","IMPRINT",EDGE,{"disambiguationData":[TD([[subQ4,-1.0]])],"derivedFrom":subQ3}),-1.0]])]});}
            var Q55;
            {var subQ1=sQuery(id+"F0.wireOp",EDGE,"E1");var subQ3=sQuery(id+"F0.wireOp",EDGE,"E80");var subQ4=makeQuery(id+"F0.imprint","INTERSECT",VERTEX,{"disambiguationData":[OD(0.0)],"derivedFrom":[subQ1,subQ3]});Q55=makeQuery(id+"F0.imprint","IMPRINT",FACE,{"disambiguationData":[TD([[makeQuery(id+"F0.imprint","IMPRINT",EDGE,{"disambiguationData":[TD([[subQ4,1.0]])],"derivedFrom":subQ3}),-1.0]])]});}
            var Q56;
            {var subQ0=sQuery(id+"F0.wireOp",EDGE,"E80");var subQ1=sQuery(id+"F0.wireOp",EDGE,"E31.0");var subQ2=makeQuery(id+"F0.imprint","INTERSECT",VERTEX,{"disambiguationData":[OD(0.0)],"derivedFrom":[subQ1,subQ0]});Q56=makeQuery(id+"F0.imprint","IMPRINT",FACE,{"disambiguationData":[TD([[makeQuery(id+"F0.imprint","IMPRINT",EDGE,{"disambiguationData":[TD([[subQ2,-1.0]])],"derivedFrom":subQ1}),-1.0]])]});}
            var Q57;
            {var subQ0=sQuery(id+"F0.wireOp",EDGE,"E80");var subQ1=sQuery(id+"F0.wireOp",EDGE,"E32.0");var subQ2=makeQuery(id+"F0.imprint","INTERSECT",VERTEX,{"disambiguationData":[OD(0.0)],"derivedFrom":[subQ1,subQ0]});Q57=makeQuery(id+"F0.imprint","IMPRINT",FACE,{"disambiguationData":[TD([[makeQuery(id+"F0.imprint","IMPRINT",EDGE,{"disambiguationData":[TD([[subQ2,-1.0]])],"derivedFrom":subQ1}),1.0]])]});}
            var Q58;
            {var subQ5=sQuery(id+"F0.wireOp",EDGE,"E80");var subQ6=sQuery(id+"F0.wireOp",EDGE,"E1");var subQ7=makeQuery(id+"F0.imprint","INTERSECT",VERTEX,{"disambiguationData":[OD(0.0)],"derivedFrom":[subQ6,subQ5]});Q58=makeQuery(id+"F0.imprint","IMPRINT",FACE,{"disambiguationData":[TD([[makeQuery(id+"F0.imprint","IMPRINT",EDGE,{"disambiguationData":[TD([[subQ7,-1.0]])],"derivedFrom":subQ6}),-1.0]])]});}
            var Q59;
            {var subQ0=sQuery(id+"F0.wireOp",EDGE,"E80");var subQ1=sQuery(id+"F0.wireOp",EDGE,"E1");var subQ2=makeQuery(id+"F0.imprint","INTERSECT",VERTEX,{"disambiguationData":[OD(0.0)],"derivedFrom":[subQ1,subQ0]});Q59=makeQuery(id+"F0.imprint","IMPRINT",FACE,{"disambiguationData":[TD([[makeQuery(id+"F0.imprint","IMPRINT",EDGE,{"disambiguationData":[TD([[subQ2,-1.0]])],"derivedFrom":subQ1}),1.0]])]});}
            var Q60;
            {var subQ0=sQuery(id+"F0.wireOp",EDGE,"E53.left");var subQ1=sQuery(id+"F0.wireOp",EDGE,"E32.0");var subQ2=makeQuery(id+"F0.imprint","INTERSECT",VERTEX,{"derivedFrom":[subQ1,subQ0]});Q60=makeQuery(id+"F0.imprint","IMPRINT",FACE,{"disambiguationData":[TD([[makeQuery(id+"F0.imprint","IMPRINT",EDGE,{"disambiguationData":[TD([[subQ2,-1.0]])],"derivedFrom":subQ1}),1.0]])]});}
            var Q61;
            {var subQ0=sQuery(id+"F0.wireOp",EDGE,"E80");var subQ1=sQuery(id+"F0.wireOp",EDGE,"E32.0");var subQ2=makeQuery(id+"F0.imprint","INTERSECT",VERTEX,{"disambiguationData":[OD(1.0)],"derivedFrom":[subQ1,subQ0]});Q61=makeQuery(id+"F0.imprint","IMPRINT",FACE,{"disambiguationData":[TD([[makeQuery(id+"F0.imprint","IMPRINT",EDGE,{"disambiguationData":[TD([[subQ2,-1.0]])],"derivedFrom":subQ1}),-1.0]])]});}
            var Q62;
            {var subQ1=sQuery(id+"F0.wireOp",EDGE,"E32.0");var subQ5=sQuery(id+"F0.wireOp",EDGE,"E53.left");var subQ6=makeQuery(id+"F0.imprint","INTERSECT",VERTEX,{"derivedFrom":[subQ1,subQ5]});Q62=makeQuery(id+"F0.imprint","IMPRINT",FACE,{"disambiguationData":[TD([[makeQuery(id+"F0.imprint","IMPRINT",EDGE,{"disambiguationData":[TD([[subQ6,-1.0]])],"derivedFrom":subQ1}),-1.0]])]});}
            var Q63;
            {var subQ0=sQuery(id+"F0.wireOp",EDGE,"E84");var subQ1=sQuery(id+"F0.wireOp",EDGE,"E1");var subQ2=makeQuery(id+"F0.imprint","INTERSECT",VERTEX,{"disambiguationData":[OD(1.0)],"derivedFrom":[subQ1,subQ0]});Q63=makeQuery(id+"F0.imprint","IMPRINT",FACE,{"disambiguationData":[TD([[makeQuery(id+"F0.imprint","IMPRINT",EDGE,{"disambiguationData":[TD([[subQ2,-1.0]])],"derivedFrom":subQ1}),1.0]])]});}
            var Q64;
            {var subQ0=sQuery(id+"F0.wireOp",EDGE,"E80");var subQ1=sQuery(id+"F0.wireOp",EDGE,"E31.0");var subQ2=makeQuery(id+"F0.imprint","INTERSECT",VERTEX,{"disambiguationData":[OD(1.0)],"derivedFrom":[subQ1,subQ0]});Q64=makeQuery(id+"F0.imprint","IMPRINT",FACE,{"disambiguationData":[TD([[makeQuery(id+"F0.imprint","IMPRINT",EDGE,{"disambiguationData":[TD([[subQ2,-1.0]])],"derivedFrom":subQ1}),1.0]])]});}
            var Q65;
            {var subQ0=sQuery(id+"F0.wireOp",EDGE,"E84");var subQ1=sQuery(id+"F0.wireOp",EDGE,"E1");var subQ2=makeQuery(id+"F0.imprint","INTERSECT",VERTEX,{"disambiguationData":[OD(1.0)],"derivedFrom":[subQ1,subQ0]});Q65=makeQuery(id+"F0.imprint","IMPRINT",FACE,{"disambiguationData":[TD([[makeQuery(id+"F0.imprint","IMPRINT",EDGE,{"disambiguationData":[TD([[subQ2,-1.0]])],"derivedFrom":subQ1}),-1.0]])]});}
            var Q66;
            {var subQ5=sQuery(id+"F0.wireOp",EDGE,"E31.0");var subQ7=sQuery(id+"F0.wireOp",EDGE,"E53.top");var subQ8=makeQuery(id+"F0.imprint","INTERSECT",VERTEX,{"derivedFrom":[subQ5,subQ7]});Q66=makeQuery(id+"F0.imprint","IMPRINT",FACE,{"disambiguationData":[TD([[makeQuery(id+"F0.imprint","IMPRINT",EDGE,{"disambiguationData":[TD([[subQ8,-1.0]])],"derivedFrom":subQ5}),1.0]])]});}
            var Q67;
            {var subQ0=sQuery(id+"F0.wireOp",EDGE,"E53.top");var subQ1=sQuery(id+"F0.wireOp",EDGE,"E31.0");var subQ2=makeQuery(id+"F0.imprint","INTERSECT",VERTEX,{"derivedFrom":[subQ1,subQ0]});Q67=makeQuery(id+"F0.imprint","IMPRINT",FACE,{"disambiguationData":[TD([[makeQuery(id+"F0.imprint","IMPRINT",EDGE,{"disambiguationData":[TD([[subQ2,-1.0]])],"derivedFrom":subQ1}),-1.0]])]});}
            var Q68;
            {var subQ0=sQuery(id+"F0.wireOp",EDGE,"E53.left");var subQ1=sQuery(id+"F0.wireOp",EDGE,"E34.0");var subQ2=makeQuery(id+"F0.imprint","INTERSECT",VERTEX,{"derivedFrom":[subQ1,subQ0]});Q68=makeQuery(id+"F0.imprint","IMPRINT",FACE,{"disambiguationData":[TD([[makeQuery(id+"F0.imprint","IMPRINT",EDGE,{"disambiguationData":[TD([[subQ2,-1.0]])],"derivedFrom":subQ1}),1.0]])]});}
            var Q69;
            {var subQ4=sQuery(id+"F0.wireOp",EDGE,"E0");var subQ8=sQuery(id+"F0.wireOp",EDGE,"E83");var subQ10=makeQuery(id+"F0.imprint","INTERSECT",VERTEX,{"disambiguationData":[OD(1.0)],"derivedFrom":[subQ4,subQ8]});Q69=makeQuery(id+"F0.imprint","IMPRINT",FACE,{"disambiguationData":[TD([[makeQuery(id+"F0.imprint","IMPRINT",EDGE,{"disambiguationData":[TD([[subQ10,-1.0]])],"derivedFrom":subQ4}),1.0]])]});}
            var Q70;
            {var subQ0=sQuery(id+"F0.wireOp",EDGE,"E79");var subQ1=sQuery(id+"F0.wireOp",EDGE,"E34.0");var subQ2=makeQuery(id+"F0.imprint","INTERSECT",VERTEX,{"disambiguationData":[OD(0.0)],"derivedFrom":[subQ1,subQ0]});Q70=makeQuery(id+"F0.imprint","IMPRINT",FACE,{"disambiguationData":[TD([[makeQuery(id+"F0.imprint","IMPRINT",EDGE,{"disambiguationData":[TD([[subQ2,-1.0]])],"derivedFrom":subQ1}),1.0]])]});}
            var Q71;
            {var subQ0=sQuery(id+"F0.wireOp",EDGE,"E79");var subQ1=sQuery(id+"F0.wireOp",EDGE,"E34.0");var subQ2=makeQuery(id+"F0.imprint","INTERSECT",VERTEX,{"disambiguationData":[OD(0.0)],"derivedFrom":[subQ1,subQ0]});Q71=makeQuery(id+"F0.imprint","IMPRINT",FACE,{"disambiguationData":[TD([[makeQuery(id+"F0.imprint","IMPRINT",EDGE,{"disambiguationData":[TD([[subQ2,-1.0]])],"derivedFrom":subQ1}),-1.0]])]});}
            var Q72;
            {var subQ0=sQuery(id+"F0.wireOp",EDGE,"E2.bottom");var subQ10=makeQuery(id+"F0.imprint","INTERSECT",VERTEX,{"derivedFrom":[subQ0,sQuery(id+"F0.wireOp",EDGE,"E20")]});Q72=makeQuery(id+"F0.imprint","IMPRINT",FACE,{"disambiguationData":[TD([[makeQuery(id+"F0.imprint","IMPRINT",EDGE,{"disambiguationData":[TD([[subQ10,1.0]])],"derivedFrom":subQ0}),-1.0]])]});}
            var Q73;
            {var subQ0=sQuery(id+"F0.wireOp",EDGE,"E22");Q73=makeQuery(id+"F0.imprint","IMPRINT",FACE,{"disambiguationData":[TD([[makeQuery(id+"F0.imprint","IMPRINT",EDGE,{"derivedFrom":subQ0}),1.0]])]});}
            var Q74;
            Q74=makeQuery(id+"F0.imprint","IMPRINT",FACE,{"disambiguationData":[TD([[makeQuery(id+"F0.imprint","IMPRINT",EDGE,{"derivedFrom":sQuery(id+"F0.wireOp",EDGE,"E65")}),-1.0]])]});
            var Q75;
            Q75=makeQuery(id+"F0.imprint","IMPRINT",FACE,{"disambiguationData":[TD([[makeQuery(id+"F0.imprint","IMPRINT",EDGE,{"derivedFrom":sQuery(id+"F0.wireOp",EDGE,"E13")}),-1.0]])]});
            var Q76;
            {var subQ0=sQuery(id+"F0.wireOp",EDGE,"E32.0");var subQ1=sQuery(id+"F0.wireOp",EDGE,"E2.right");var subQ2=makeQuery(id+"F0.imprint","INTERSECT",VERTEX,{"derivedFrom":[subQ1,subQ0]});Q76=makeQuery(id+"F0.imprint","IMPRINT",FACE,{"disambiguationData":[TD([[makeQuery(id+"F0.imprint","IMPRINT",EDGE,{"disambiguationData":[TD([[subQ2,1.0]])],"derivedFrom":subQ1}),1.0]])]});}
            var Q77;
            {var subQ0=sQuery(id+"F0.wireOp",EDGE,"E33.0");var subQ5=sQuery(id+"F0.wireOp",EDGE,"E2.left");var subQ6=makeQuery(id+"F0.imprint","INTERSECT",VERTEX,{"derivedFrom":[subQ5,subQ0]});Q77=makeQuery(id+"F0.imprint","IMPRINT",FACE,{"disambiguationData":[TD([[makeQuery(id+"F0.imprint","IMPRINT",EDGE,{"disambiguationData":[TD([[subQ6,1.0]])],"derivedFrom":subQ5}),-1.0]])]});}
            var Q78;
            Q78=makeQuery(id+"F0.imprint","IMPRINT",FACE,{"disambiguationData":[TD([[makeQuery(id+"F0.imprint","IMPRINT",EDGE,{"derivedFrom":sQuery(id+"F0.wireOp",EDGE,"E74")}),-1.0]])]});
            var Q79;
            {var subQ0=sQuery(id+"F0.wireOp",EDGE,"E33.0");var subQ1=sQuery(id+"F0.wireOp",EDGE,"E2.left");var subQ2=makeQuery(id+"F0.imprint","INTERSECT",VERTEX,{"derivedFrom":[subQ1,subQ0]});Q79=makeQuery(id+"F0.imprint","IMPRINT",FACE,{"disambiguationData":[TD([[makeQuery(id+"F0.imprint","IMPRINT",EDGE,{"disambiguationData":[TD([[subQ2,1.0]])],"derivedFrom":subQ1}),1.0]])]});}
            var Q80;
            {var subQ7=sQuery(id+"F0.wireOp",EDGE,"E58");var subQ10=sQuery(id+"F0.wireOp",EDGE,"E1");var subQ12=makeQuery(id+"F0.imprint","INTERSECT",VERTEX,{"derivedFrom":[subQ10,subQ7]});Q80=makeQuery(id+"F0.imprint","IMPRINT",FACE,{"disambiguationData":[TD([[makeQuery(id+"F0.imprint","IMPRINT",EDGE,{"disambiguationData":[TD([[subQ12,-1.0]])],"derivedFrom":subQ10}),1.0]])]});}
            var Q81;
            {var subQ1=sQuery(id+"F0.wireOp",EDGE,"E2.left");var subQ13=makeQuery(id+"F0.imprint","INTERSECT",VERTEX,{"derivedFrom":[subQ1,sQuery(id+"F0.wireOp",EDGE,"E27")]});Q81=makeQuery(id+"F0.imprint","IMPRINT",FACE,{"disambiguationData":[TD([[makeQuery(id+"F0.imprint","IMPRINT",EDGE,{"disambiguationData":[TD([[subQ13,1.0]])],"derivedFrom":subQ1}),1.0]])]});}
            var Q82;
            {var subQ0=sQuery(id+"F0.wireOp",EDGE,"E30");Q82=makeQuery(id+"F0.imprint","IMPRINT",FACE,{"disambiguationData":[TD([[makeQuery(id+"F0.imprint","IMPRINT",EDGE,{"derivedFrom":subQ0}),1.0]])]});}
            var Q83;
            {var subQ0=sQuery(id+"F0.wireOp",EDGE,"E29");Q83=makeQuery(id+"F0.imprint","IMPRINT",FACE,{"disambiguationData":[TD([[makeQuery(id+"F0.imprint","IMPRINT",EDGE,{"derivedFrom":subQ0}),-1.0]])]});}
            var Q84;
            {var subQ0=sQuery(id+"F0.wireOp",EDGE,"E32.0");var subQ1=sQuery(id+"F0.wireOp",EDGE,"E2.right");var subQ2=makeQuery(id+"F0.imprint","INTERSECT",VERTEX,{"derivedFrom":[subQ1,subQ0]});Q84=makeQuery(id+"F0.imprint","IMPRINT",FACE,{"disambiguationData":[TD([[makeQuery(id+"F0.imprint","IMPRINT",EDGE,{"disambiguationData":[TD([[subQ2,1.0]])],"derivedFrom":subQ1}),-1.0]])]});}
            var Q85;
            {var subQ1=sQuery(id+"F0.wireOp",EDGE,"E4");var subQ8=sQuery(id+"F0.wireOp",EDGE,"E1");var subQ9=makeQuery(id+"F0.imprint","INTERSECT",VERTEX,{"derivedFrom":[subQ8,subQ1]});Q85=makeQuery(id+"F0.imprint","IMPRINT",FACE,{"disambiguationData":[TD([[makeQuery(id+"F0.imprint","IMPRINT",EDGE,{"disambiguationData":[TD([[subQ9,-1.0]])],"derivedFrom":subQ8}),-1.0]])]});}
            var Q86;
            {var subQ0=sQuery(id+"F0.wireOp",EDGE,"E34.0");var subQ1=sQuery(id+"F0.wireOp",EDGE,"E2.right");var subQ2=makeQuery(id+"F0.imprint","INTERSECT",VERTEX,{"derivedFrom":[subQ1,subQ0]});Q86=makeQuery(id+"F0.imprint","IMPRINT",FACE,{"disambiguationData":[TD([[makeQuery(id+"F0.imprint","IMPRINT",EDGE,{"disambiguationData":[TD([[subQ2,-1.0]])],"derivedFrom":subQ1}),-1.0]])]});}
            var Q87;
            {var subQ0=sQuery(id+"F0.wireOp",EDGE,"E31.0");var subQ1=sQuery(id+"F0.wireOp",EDGE,"E2.left");var subQ2=makeQuery(id+"F0.imprint","INTERSECT",VERTEX,{"derivedFrom":[subQ1,subQ0]});Q87=makeQuery(id+"F0.imprint","IMPRINT",FACE,{"disambiguationData":[TD([[makeQuery(id+"F0.imprint","IMPRINT",EDGE,{"disambiguationData":[TD([[subQ2,-1.0]])],"derivedFrom":subQ1}),1.0]])]});}
            var Q88;
            {var subQ0=sQuery(id+"F0.wireOp",EDGE,"E2.left");var subQ4=sQuery(id+"F0.wireOp",EDGE,"E31.0");var subQ5=makeQuery(id+"F0.imprint","INTERSECT",VERTEX,{"derivedFrom":[subQ0,subQ4]});Q88=makeQuery(id+"F0.imprint","IMPRINT",FACE,{"disambiguationData":[TD([[makeQuery(id+"F0.imprint","IMPRINT",EDGE,{"disambiguationData":[TD([[subQ5,-1.0]])],"derivedFrom":subQ0}),-1.0]])]});}
            var Q89;
            {var subQ0=sQuery(id+"F0.wireOp",EDGE,"E26");Q89=makeQuery(id+"F0.imprint","IMPRINT",FACE,{"disambiguationData":[TD([[makeQuery(id+"F0.imprint","IMPRINT",EDGE,{"derivedFrom":subQ0}),1.0]])]});}
            var Q90;
            {var subQ0=sQuery(id+"F0.wireOp",EDGE,"E31.0");var subQ1=sQuery(id+"F0.wireOp",EDGE,"E2.bottom");var subQ2=makeQuery(id+"F0.imprint","INTERSECT",VERTEX,{"derivedFrom":[subQ1,subQ0]});Q90=makeQuery(id+"F0.imprint","IMPRINT",FACE,{"disambiguationData":[TD([[makeQuery(id+"F0.imprint","IMPRINT",EDGE,{"disambiguationData":[TD([[subQ2,-1.0]])],"derivedFrom":subQ1}),-1.0]])]});}
            var Q91;
            {var subQ0=sQuery(id+"F0.wireOp",EDGE,"E34.0");var subQ1=sQuery(id+"F0.wireOp",EDGE,"E2.bottom");var subQ2=makeQuery(id+"F0.imprint","INTERSECT",VERTEX,{"derivedFrom":[subQ1,subQ0]});Q91=makeQuery(id+"F0.imprint","IMPRINT",FACE,{"disambiguationData":[TD([[makeQuery(id+"F0.imprint","IMPRINT",EDGE,{"disambiguationData":[TD([[subQ2,1.0]])],"derivedFrom":subQ1}),1.0]])]});}
            var Q92;
            {var subQ0=sQuery(id+"F0.wireOp",EDGE,"E33.0");var subQ5=sQuery(id+"F0.wireOp",EDGE,"E2.top");var subQ8=makeQuery(id+"F0.imprint","INTERSECT",VERTEX,{"derivedFrom":[subQ5,subQ0]});Q92=makeQuery(id+"F0.imprint","IMPRINT",FACE,{"disambiguationData":[TD([[makeQuery(id+"F0.imprint","IMPRINT",EDGE,{"disambiguationData":[TD([[subQ8,-1.0]])],"derivedFrom":subQ5}),-1.0]])]});}
            var Q93;
            Q93=makeQuery(id+"F0.imprint","IMPRINT",FACE,{"disambiguationData":[TD([[makeQuery(id+"F0.imprint","IMPRINT",EDGE,{"derivedFrom":sQuery(id+"F0.wireOp",EDGE,"E69")}),-1.0]])]});
            var Q94;
            {var subQ0=sQuery(id+"F0.wireOp",EDGE,"E31.0");var subQ5=sQuery(id+"F0.wireOp",EDGE,"E2.bottom");var subQ8=makeQuery(id+"F0.imprint","INTERSECT",VERTEX,{"derivedFrom":[subQ5,subQ0]});Q94=makeQuery(id+"F0.imprint","IMPRINT",FACE,{"disambiguationData":[TD([[makeQuery(id+"F0.imprint","IMPRINT",EDGE,{"disambiguationData":[TD([[subQ8,-1.0]])],"derivedFrom":subQ5}),1.0]])]});}
            var Q95;
            {var subQ0=sQuery(id+"F0.wireOp",EDGE,"E20");Q95=makeQuery(id+"F0.imprint","IMPRINT",FACE,{"disambiguationData":[TD([[makeQuery(id+"F0.imprint","IMPRINT",EDGE,{"derivedFrom":subQ0}),1.0]])]});}
            var Q96;
            {var subQ1=sQuery(id+"F0.wireOp",EDGE,"E5");var subQ8=sQuery(id+"F0.wireOp",EDGE,"E0");var subQ9=makeQuery(id+"F0.imprint","INTERSECT",VERTEX,{"derivedFrom":[subQ8,subQ1]});Q96=makeQuery(id+"F0.imprint","IMPRINT",FACE,{"disambiguationData":[TD([[makeQuery(id+"F0.imprint","IMPRINT",EDGE,{"disambiguationData":[TD([[subQ9,-1.0]])],"derivedFrom":subQ8}),-1.0]])]});}
            var Q97;
            {var subQ0=sQuery(id+"F0.wireOp",EDGE,"E33.0");var subQ1=sQuery(id+"F0.wireOp",EDGE,"E2.top");var subQ2=makeQuery(id+"F0.imprint","INTERSECT",VERTEX,{"derivedFrom":[subQ1,subQ0]});Q97=makeQuery(id+"F0.imprint","IMPRINT",FACE,{"disambiguationData":[TD([[makeQuery(id+"F0.imprint","IMPRINT",EDGE,{"disambiguationData":[TD([[subQ2,-1.0]])],"derivedFrom":subQ1}),1.0]])]});}
            var Q98;
            Q98=makeQuery(id+"F0.imprint","IMPRINT",FACE,{"disambiguationData":[TD([[makeQuery(id+"F0.imprint","IMPRINT",EDGE,{"derivedFrom":sQuery(id+"F0.wireOp",EDGE,"E15")}),-1.0]])]});
            var Q99;
            {var subQ1=sQuery(id+"F0.wireOp",EDGE,"E4");var subQ8=sQuery(id+"F0.wireOp",EDGE,"E1");var subQ9=makeQuery(id+"F0.imprint","INTERSECT",VERTEX,{"derivedFrom":[subQ8,subQ1]});Q99=makeQuery(id+"F0.imprint","IMPRINT",FACE,{"disambiguationData":[TD([[makeQuery(id+"F0.imprint","IMPRINT",EDGE,{"disambiguationData":[TD([[subQ9,-1.0]])],"derivedFrom":subQ8}),1.0]])]});}
            var Q100;
            Q100=makeQuery(id+"F0.imprint","IMPRINT",FACE,{"disambiguationData":[TD([[makeQuery(id+"F0.imprint","IMPRINT",EDGE,{"derivedFrom":sQuery(id+"F0.wireOp",EDGE,"E11")}),-1.0]])]});
            var Q101;
            {var subQ1=sQuery(id+"F0.wireOp",EDGE,"E5");var subQ10=sQuery(id+"F0.wireOp",EDGE,"E0");var subQ11=makeQuery(id+"F0.imprint","INTERSECT",VERTEX,{"derivedFrom":[subQ10,subQ1]});Q101=makeQuery(id+"F0.imprint","IMPRINT",FACE,{"disambiguationData":[TD([[makeQuery(id+"F0.imprint","IMPRINT",EDGE,{"disambiguationData":[TD([[subQ11,-1.0]])],"derivedFrom":subQ10}),1.0]])]});}
            var Q102;
            Q102=makeQuery(id+"F0.imprint","IMPRINT",FACE,{"disambiguationData":[TD([[makeQuery(id+"F0.imprint","IMPRINT",EDGE,{"derivedFrom":sQuery(id+"F0.wireOp",EDGE,"E14")}),-1.0]])]});
            var Q103;
            {var subQ0=sQuery(id+"F0.wireOp",EDGE,"E34.0");var subQ1=sQuery(id+"F0.wireOp",EDGE,"E2.bottom");var subQ2=makeQuery(id+"F0.imprint","INTERSECT",VERTEX,{"derivedFrom":[subQ1,subQ0]});Q103=makeQuery(id+"F0.imprint","IMPRINT",FACE,{"disambiguationData":[TD([[makeQuery(id+"F0.imprint","IMPRINT",EDGE,{"disambiguationData":[TD([[subQ2,1.0]])],"derivedFrom":subQ1}),-1.0]])]});}
            var Q104;
            {var subQ8=sQuery(id+"F0.wireOp",EDGE,"E0");var subQ10=sQuery(id+"F0.wireOp",EDGE,"E57");var subQ11=makeQuery(id+"F0.imprint","INTERSECT",VERTEX,{"derivedFrom":[subQ8,subQ10]});Q104=makeQuery(id+"F0.imprint","IMPRINT",FACE,{"disambiguationData":[TD([[makeQuery(id+"F0.imprint","IMPRINT",EDGE,{"disambiguationData":[TD([[subQ11,-1.0]])],"derivedFrom":subQ8}),-1.0]])]});}
            var Q105;
            Q105=makeQuery(id+"F0.imprint","IMPRINT",FACE,{"disambiguationData":[TD([[makeQuery(id+"F0.imprint","IMPRINT",EDGE,{"derivedFrom":sQuery(id+"F0.wireOp",EDGE,"E61")}),-1.0]])]});
            var Q106;
            {var subQ8=sQuery(id+"F0.wireOp",EDGE,"E1");var subQ10=sQuery(id+"F0.wireOp",EDGE,"E58");var subQ12=makeQuery(id+"F0.imprint","INTERSECT",VERTEX,{"derivedFrom":[subQ8,subQ10]});Q106=makeQuery(id+"F0.imprint","IMPRINT",FACE,{"disambiguationData":[TD([[makeQuery(id+"F0.imprint","IMPRINT",EDGE,{"disambiguationData":[TD([[subQ12,-1.0]])],"derivedFrom":subQ8}),-1.0]])]});}
            var Q107;
            {var subQ0=sQuery(id+"F0.wireOp",EDGE,"E32.0");var subQ5=sQuery(id+"F0.wireOp",EDGE,"E2.top");var subQ6=makeQuery(id+"F0.imprint","INTERSECT",VERTEX,{"derivedFrom":[subQ5,subQ0]});Q107=makeQuery(id+"F0.imprint","IMPRINT",FACE,{"disambiguationData":[TD([[makeQuery(id+"F0.imprint","IMPRINT",EDGE,{"disambiguationData":[TD([[subQ6,1.0]])],"derivedFrom":subQ5}),-1.0]])]});}
            var Q108;
            {var subQ1=sQuery(id+"F0.wireOp",EDGE,"E2.top");var subQ8=makeQuery(id+"F0.imprint","INTERSECT",VERTEX,{"derivedFrom":[subQ1,sQuery(id+"F0.wireOp",EDGE,"E25")]});Q108=makeQuery(id+"F0.imprint","IMPRINT",FACE,{"disambiguationData":[TD([[makeQuery(id+"F0.imprint","IMPRINT",EDGE,{"disambiguationData":[TD([[subQ8,1.0]])],"derivedFrom":subQ1}),1.0]])]});}
            var Q109;
            {var subQ1=sQuery(id+"F0.wireOp",EDGE,"E2.right");var subQ12=makeQuery(id+"F0.imprint","INTERSECT",VERTEX,{"derivedFrom":[subQ1,sQuery(id+"F0.wireOp",EDGE,"E22")]});Q109=makeQuery(id+"F0.imprint","IMPRINT",FACE,{"disambiguationData":[TD([[makeQuery(id+"F0.imprint","IMPRINT",EDGE,{"disambiguationData":[TD([[subQ12,1.0]])],"derivedFrom":subQ1}),-1.0]])]});}
            var Q110;
            Q110=makeQuery(id+"F0.imprint","IMPRINT",FACE,{"disambiguationData":[TD([[makeQuery(id+"F0.imprint","IMPRINT",EDGE,{"derivedFrom":sQuery(id+"F0.wireOp",EDGE,"E12")}),-1.0]])]});
            var Q111;
            {var subQ0=sQuery(id+"F0.wireOp",EDGE,"E32.0");var subQ1=sQuery(id+"F0.wireOp",EDGE,"E2.top");var subQ2=makeQuery(id+"F0.imprint","INTERSECT",VERTEX,{"derivedFrom":[subQ1,subQ0]});Q111=makeQuery(id+"F0.imprint","IMPRINT",FACE,{"disambiguationData":[TD([[makeQuery(id+"F0.imprint","IMPRINT",EDGE,{"disambiguationData":[TD([[subQ2,1.0]])],"derivedFrom":subQ1}),1.0]])]});}
            var Q112;
            {var subQ7=sQuery(id+"F0.wireOp",EDGE,"E0");var subQ10=sQuery(id+"F0.wireOp",EDGE,"E57");var subQ11=makeQuery(id+"F0.imprint","INTERSECT",VERTEX,{"derivedFrom":[subQ7,subQ10]});Q112=makeQuery(id+"F0.imprint","IMPRINT",FACE,{"disambiguationData":[TD([[makeQuery(id+"F0.imprint","IMPRINT",EDGE,{"disambiguationData":[TD([[subQ11,-1.0]])],"derivedFrom":subQ7}),1.0]])]});}
            var Q113;
            {var subQ0=sQuery(id+"F0.wireOp",EDGE,"E24");Q113=makeQuery(id+"F0.imprint","IMPRINT",FACE,{"disambiguationData":[TD([[makeQuery(id+"F0.imprint","IMPRINT",EDGE,{"derivedFrom":subQ0}),1.0]])]});}
            var Q114;
            {var subQ0=sQuery(id+"F0.wireOp",EDGE,"E34.0");var subQ5=sQuery(id+"F0.wireOp",EDGE,"E2.right");var subQ8=makeQuery(id+"F0.imprint","INTERSECT",VERTEX,{"derivedFrom":[subQ5,subQ0]});Q114=makeQuery(id+"F0.imprint","IMPRINT",FACE,{"disambiguationData":[TD([[makeQuery(id+"F0.imprint","IMPRINT",EDGE,{"disambiguationData":[TD([[subQ8,-1.0]])],"derivedFrom":subQ5}),1.0]])]});}
            var Q115;
            {var subQ1=sQuery(id+"F0.wireOp",EDGE,"E0");var subQ3=sQuery(id+"F0.wireOp",EDGE,"E79");var subQ4=makeQuery(id+"F0.imprint","INTERSECT",VERTEX,{"disambiguationData":[OD(1.0)],"derivedFrom":[subQ1,subQ3]});Q115=makeQuery(id+"F0.imprint","IMPRINT",FACE,{"disambiguationData":[TD([[makeQuery(id+"F0.imprint","IMPRINT",EDGE,{"disambiguationData":[TD([[subQ4,-1.0]])],"derivedFrom":subQ3}),-1.0]])]});}
            var Q116;
            {var subQ1=sQuery(id+"F0.wireOp",EDGE,"E0");var subQ3=sQuery(id+"F0.wireOp",EDGE,"E79");var subQ4=makeQuery(id+"F0.imprint","INTERSECT",VERTEX,{"disambiguationData":[OD(1.0)],"derivedFrom":[subQ1,subQ3]});Q116=makeQuery(id+"F0.imprint","IMPRINT",FACE,{"disambiguationData":[TD([[makeQuery(id+"F0.imprint","IMPRINT",EDGE,{"disambiguationData":[TD([[subQ4,1.0]])],"derivedFrom":subQ3}),-1.0]])]});}
            var Q117;
            {var subQ3=sQuery(id+"F0.wireOp",EDGE,"E83");var subQ8=sQuery(id+"F0.wireOp",EDGE,"E0");var subQ9=makeQuery(id+"F0.imprint","INTERSECT",VERTEX,{"disambiguationData":[OD(1.0)],"derivedFrom":[subQ8,subQ3]});Q117=makeQuery(id+"F0.imprint","IMPRINT",FACE,{"disambiguationData":[TD([[makeQuery(id+"F0.imprint","IMPRINT",EDGE,{"disambiguationData":[TD([[subQ9,-1.0]])],"derivedFrom":subQ8}),-1.0]])]});}
            var Q118;
            {var subQ0=sQuery(id+"F0.wireOp",EDGE,"E53.bottom");var subQ1=sQuery(id+"F0.wireOp",EDGE,"E33.0");var subQ2=makeQuery(id+"F0.imprint","INTERSECT",VERTEX,{"derivedFrom":[subQ1,subQ0]});Q118=makeQuery(id+"F0.imprint","IMPRINT",FACE,{"disambiguationData":[TD([[makeQuery(id+"F0.imprint","IMPRINT",EDGE,{"disambiguationData":[TD([[subQ2,-1.0]])],"derivedFrom":subQ1}),-1.0]])]});}
            var Q119;
            {var subQ0=sQuery(id+"F0.wireOp",EDGE,"E79");var subQ1=sQuery(id+"F0.wireOp",EDGE,"E33.0");var subQ2=makeQuery(id+"F0.imprint","INTERSECT",VERTEX,{"disambiguationData":[OD(0.0)],"derivedFrom":[subQ1,subQ0]});Q119=makeQuery(id+"F0.imprint","IMPRINT",FACE,{"disambiguationData":[TD([[makeQuery(id+"F0.imprint","IMPRINT",EDGE,{"disambiguationData":[TD([[subQ2,-1.0]])],"derivedFrom":subQ1}),1.0]])]});}
            var Q120;
            {var subQ0=sQuery(id+"F0.wireOp",EDGE,"E79");var subQ1=sQuery(id+"F0.wireOp",EDGE,"E33.0");var subQ2=makeQuery(id+"F0.imprint","INTERSECT",VERTEX,{"disambiguationData":[OD(0.0)],"derivedFrom":[subQ1,subQ0]});Q120=makeQuery(id+"F0.imprint","IMPRINT",FACE,{"disambiguationData":[TD([[makeQuery(id+"F0.imprint","IMPRINT",EDGE,{"disambiguationData":[TD([[subQ2,-1.0]])],"derivedFrom":subQ1}),-1.0]])]});}
            var Q121;
            {var subQ0=sQuery(id+"F0.wireOp",EDGE,"E79");var subQ1=sQuery(id+"F0.wireOp",EDGE,"E0");var subQ2=makeQuery(id+"F0.imprint","INTERSECT",VERTEX,{"disambiguationData":[OD(0.0)],"derivedFrom":[subQ1,subQ0]});Q121=makeQuery(id+"F0.imprint","IMPRINT",FACE,{"disambiguationData":[TD([[makeQuery(id+"F0.imprint","IMPRINT",EDGE,{"disambiguationData":[TD([[subQ2,-1.0]])],"derivedFrom":subQ1}),-1.0]])]});}
            var Q122;
            {var subQ0=sQuery(id+"F0.wireOp",EDGE,"E79");var subQ1=sQuery(id+"F0.wireOp",EDGE,"E0");var subQ2=makeQuery(id+"F0.imprint","INTERSECT",VERTEX,{"disambiguationData":[OD(0.0)],"derivedFrom":[subQ1,subQ0]});Q122=makeQuery(id+"F0.imprint","IMPRINT",FACE,{"disambiguationData":[TD([[makeQuery(id+"F0.imprint","IMPRINT",EDGE,{"disambiguationData":[TD([[subQ2,-1.0]])],"derivedFrom":subQ1}),1.0]])]});}
            var Q123;
            Q123=sQuery(id+"F0.wireOp",EDGE,"E81");
            var Q124;
            Q124=sQuery(id+"F0.wireOp",EDGE,"E2.left");
            var Q125;
            Q125=sQuery(id+"F0.wireOp",EDGE,"E2.bottom");
            extrude(context, id + "F1", {"entities" : qUnion([Q0, Q1, Q2, Q3, Q4, Q5, Q6, Q7, Q8, Q9, Q10, Q11, Q12, Q13, Q14, Q15, Q16, Q17, Q18, Q19, Q20, Q21, Q22, Q23, Q24, Q25, Q26, Q27, Q28, Q29, Q30, Q31, Q32, Q33, Q34, Q35, Q36, Q37, Q38, Q39, Q40, Q41, Q42, Q43, Q44, Q45, Q46, Q47, Q48, Q49, Q50, Q51, Q52, Q53, Q54, Q55, Q56, Q57, Q58, Q59, Q60, Q61, Q62, Q63, Q64, Q65, Q66, Q67, Q68, Q69, Q70, Q71, Q72, Q73, Q74, Q75, Q76, Q77, Q78, Q79, Q80, Q81, Q82, Q83, Q84, Q85, Q86, Q87, Q88, Q89, Q90, Q91, Q92, Q93, Q94, Q95, Q96, Q97, Q98, Q99, Q100, Q101, Q102, Q103, Q104, Q105, Q106, Q107, Q108, Q109, Q110, Q111, Q112, Q113, Q114, Q115, Q116, Q117, Q118, Q119, Q120, Q121, Q122]), "surfaceEntities" : qUnion([Q123, Q124, Q125]), "depth" : 4 * mm, "offsetDistance" : 25 * mm});
        }
        {
            var Q0;
            Q0=makeQuery(id+"F1.opExtrude","SWEPT_EDGE",EDGE,{"disambiguationData":[OSD([sQuery(id+"F0.wireOp",EDGE,"E2.bottom"),sQuery(id+"F0.wireOp",EDGE,"E31.0")])]});
            var Q1;
            Q1=makeQuery(id+"F1.opExtrude","SWEPT_EDGE",EDGE,{"disambiguationData":[OSD([sQuery(id+"F0.wireOp",EDGE,"E6"),sQuery(id+"F0.wireOp",EDGE,"E31.0")])]});
            var Q2;
            Q2=makeQuery(id+"F1.opExtrude","SWEPT_EDGE",EDGE,{"disambiguationData":[OSD([sQuery(id+"F0.wireOp",EDGE,"E6"),sQuery(id+"F0.wireOp",EDGE,"E32.0")])]});
            var Q3;
            Q3=makeQuery(id+"F1.opExtrude","SWEPT_EDGE",EDGE,{"disambiguationData":[OSD([sQuery(id+"F0.wireOp",EDGE,"E2.right"),sQuery(id+"F0.wireOp",EDGE,"E32.0")])]});
            var Q4;
            Q4=makeQuery(id+"F1.opExtrude","SWEPT_EDGE",EDGE,{"disambiguationData":[OSD([sQuery(id+"F0.wireOp",EDGE,"E2.right"),sQuery(id+"F0.wireOp",EDGE,"E34.0")])]});
            var Q5;
            Q5=makeQuery(id+"F1.opExtrude","SWEPT_EDGE",EDGE,{"disambiguationData":[OSD([sQuery(id+"F0.wireOp",EDGE,"E5"),sQuery(id+"F0.wireOp",EDGE,"E34.0")])]});
            var Q6;
            Q6=makeQuery(id+"F1.opExtrude","SWEPT_EDGE",EDGE,{"disambiguationData":[OSD([sQuery(id+"F0.wireOp",EDGE,"E5"),sQuery(id+"F0.wireOp",EDGE,"E33.0")])]});
            var Q7;
            Q7=makeQuery(id+"F1.opExtrude","SWEPT_EDGE",EDGE,{"disambiguationData":[OSD([sQuery(id+"F0.wireOp",EDGE,"E2.top"),sQuery(id+"F0.wireOp",EDGE,"E33.0")])]});
            var Q8;
            Q8=makeQuery(id+"F1.opExtrude","SWEPT_EDGE",EDGE,{"disambiguationData":[OSD([sQuery(id+"F0.wireOp",EDGE,"E2.top"),sQuery(id+"F0.wireOp",EDGE,"E32.0")])]});
            var Q9;
            Q9=makeQuery(id+"F1.opExtrude","SWEPT_EDGE",EDGE,{"disambiguationData":[OSD([sQuery(id+"F0.wireOp",EDGE,"E4"),sQuery(id+"F0.wireOp",EDGE,"E32.0")])]});
            var Q10;
            Q10=makeQuery(id+"F1.opExtrude","SWEPT_EDGE",EDGE,{"disambiguationData":[OSD([sQuery(id+"F0.wireOp",EDGE,"E4"),sQuery(id+"F0.wireOp",EDGE,"E31.0")])]});
            var Q11;
            Q11=makeQuery(id+"F1.opExtrude","SWEPT_EDGE",EDGE,{"disambiguationData":[OSD([sQuery(id+"F0.wireOp",EDGE,"E2.left"),sQuery(id+"F0.wireOp",EDGE,"E31.0")])]});
            var Q12;
            Q12=makeQuery(id+"F1.opExtrude","SWEPT_EDGE",EDGE,{"disambiguationData":[OSD([sQuery(id+"F0.wireOp",EDGE,"E2.left"),sQuery(id+"F0.wireOp",EDGE,"E33.0")])]});
            var Q13;
            Q13=makeQuery(id+"F1.opExtrude","SWEPT_EDGE",EDGE,{"disambiguationData":[OSD([sQuery(id+"F0.wireOp",EDGE,"E3"),sQuery(id+"F0.wireOp",EDGE,"E33.0")])]});
            var Q14;
            Q14=makeQuery(id+"F1.opExtrude","SWEPT_EDGE",EDGE,{"disambiguationData":[OSD([sQuery(id+"F0.wireOp",EDGE,"E3"),sQuery(id+"F0.wireOp",EDGE,"E34.0")])]});
            var Q15;
            Q15=makeQuery(id+"F1.opExtrude","SWEPT_EDGE",EDGE,{"disambiguationData":[OSD([sQuery(id+"F0.wireOp",EDGE,"E2.bottom"),sQuery(id+"F0.wireOp",EDGE,"E34.0")])]});
            fillet(context, id + "F2", {"entities" : qUnion([Q0, Q1, Q2, Q3, Q4, Q5, Q6, Q7, Q8, Q9, Q10, Q11, Q12, Q13, Q14, Q15]), "radius" : 5 * mm, "tangentPropagation" : true, "allowEdgeOverflow" : false});
        }
        {
            var Q0;
            Q0=makeQuery(id+"F1.opExtrude","SWEPT_EDGE",EDGE,{"disambiguationData":[OSD([sQuery(id+"F0.wireOp",EDGE,"E0"),sQuery(id+"F0.wireOp",EDGE,"E55.left"),sQuery(id+"F0.wireOp",EDGE,"E56.top")])]});
            var Q1;
            Q1=makeQuery(id+"F1.opExtrude","SWEPT_EDGE",EDGE,{"disambiguationData":[OSD([sQuery(id+"F0.wireOp",EDGE,"E1"),sQuery(id+"F0.wireOp",EDGE,"E55.right"),sQuery(id+"F0.wireOp",EDGE,"E56.top")])]});
            var Q2;
            Q2=makeQuery(id+"F1.opExtrude","SWEPT_EDGE",EDGE,{"disambiguationData":[OSD([sQuery(id+"F0.wireOp",EDGE,"E1"),sQuery(id+"F0.wireOp",EDGE,"E55.left"),sQuery(id+"F0.wireOp",EDGE,"E56.bottom")])]});
            var Q3;
            Q3=makeQuery(id+"F1.opExtrude","SWEPT_EDGE",EDGE,{"disambiguationData":[OSD([sQuery(id+"F0.wireOp",EDGE,"E0"),sQuery(id+"F0.wireOp",EDGE,"E55.right"),sQuery(id+"F0.wireOp",EDGE,"E56.bottom")])]});
            var Q4;
            Q4=makeQuery(id+"F1.opExtrude","SWEPT_EDGE",EDGE,{"disambiguationData":[OSD([sQuery(id+"F0.wireOp",EDGE,"E54.left"),sQuery(id+"F0.wireOp",EDGE,"E81")])]});
            var Q5;
            Q5=makeQuery(id+"F1.opExtrude","SWEPT_EDGE",EDGE,{"disambiguationData":[OSD([sQuery(id+"F0.wireOp",EDGE,"E54.left"),sQuery(id+"F0.wireOp",EDGE,"E56.top"),sQuery(id+"F0.wireOp",EDGE,"E56.left")])]});
            var Q6;
            Q6=makeQuery(id+"F1.opExtrude","SWEPT_EDGE",EDGE,{"disambiguationData":[OSD([sQuery(id+"F0.wireOp",EDGE,"E54.left"),sQuery(id+"F0.wireOp",EDGE,"E78")])]});
            var Q7;
            Q7=makeQuery(id+"F1.opExtrude","SWEPT_EDGE",EDGE,{"disambiguationData":[OSD([sQuery(id+"F0.wireOp",EDGE,"E54.bottom"),sQuery(id+"F0.wireOp",EDGE,"E78")])]});
            var Q8;
            Q8=makeQuery(id+"F1.opExtrude","SWEPT_EDGE",EDGE,{"disambiguationData":[OSD([sQuery(id+"F0.wireOp",EDGE,"E54.bottom"),sQuery(id+"F0.wireOp",EDGE,"E55.top"),sQuery(id+"F0.wireOp",EDGE,"E55.right")])]});
            var Q9;
            Q9=makeQuery(id+"F1.opExtrude","SWEPT_EDGE",EDGE,{"disambiguationData":[OSD([sQuery(id+"F0.wireOp",EDGE,"E54.left"),sQuery(id+"F0.wireOp",EDGE,"E56.bottom"),sQuery(id+"F0.wireOp",EDGE,"E56.left")])]});
            var Q10;
            Q10=makeQuery(id+"F1.opExtrude","SWEPT_EDGE",EDGE,{"disambiguationData":[OSD([sQuery(id+"F0.wireOp",EDGE,"E54.top"),sQuery(id+"F0.wireOp",EDGE,"E55.bottom"),sQuery(id+"F0.wireOp",EDGE,"E55.right")])]});
            var Q11;
            Q11=makeQuery(id+"F1.opExtrude","SWEPT_EDGE",EDGE,{"disambiguationData":[OSD([sQuery(id+"F0.wireOp",EDGE,"E54.top"),sQuery(id+"F0.wireOp",EDGE,"E81")])]});
            var Q12;
            Q12=makeQuery(id+"F1.opExtrude","SWEPT_EDGE",EDGE,{"disambiguationData":[OSD([sQuery(id+"F0.wireOp",EDGE,"E54.top"),sQuery(id+"F0.wireOp",EDGE,"E55.bottom"),sQuery(id+"F0.wireOp",EDGE,"E55.left")])]});
            var Q13;
            Q13=makeQuery(id+"F1.opExtrude","SWEPT_EDGE",EDGE,{"disambiguationData":[OSD([sQuery(id+"F0.wireOp",EDGE,"E54.top"),sQuery(id+"F0.wireOp",EDGE,"E80")])]});
            var Q14;
            Q14=makeQuery(id+"F1.opExtrude","SWEPT_EDGE",EDGE,{"disambiguationData":[OSD([sQuery(id+"F0.wireOp",EDGE,"E54.right"),sQuery(id+"F0.wireOp",EDGE,"E80")])]});
            var Q15;
            Q15=makeQuery(id+"F1.opExtrude","SWEPT_EDGE",EDGE,{"disambiguationData":[OSD([sQuery(id+"F0.wireOp",EDGE,"E54.right"),sQuery(id+"F0.wireOp",EDGE,"E56.bottom"),sQuery(id+"F0.wireOp",EDGE,"E56.right")])]});
            var Q16;
            Q16=makeQuery(id+"F1.opExtrude","SWEPT_EDGE",EDGE,{"disambiguationData":[OSD([sQuery(id+"F0.wireOp",EDGE,"E54.right"),sQuery(id+"F0.wireOp",EDGE,"E56.top"),sQuery(id+"F0.wireOp",EDGE,"E56.right")])]});
            var Q17;
            Q17=makeQuery(id+"F1.opExtrude","SWEPT_EDGE",EDGE,{"disambiguationData":[OSD([sQuery(id+"F0.wireOp",EDGE,"E54.right"),sQuery(id+"F0.wireOp",EDGE,"E79")])]});
            var Q18;
            Q18=makeQuery(id+"F1.opExtrude","SWEPT_EDGE",EDGE,{"disambiguationData":[OSD([sQuery(id+"F0.wireOp",EDGE,"E54.bottom"),sQuery(id+"F0.wireOp",EDGE,"E79")])]});
            var Q19;
            Q19=makeQuery(id+"F1.opExtrude","SWEPT_EDGE",EDGE,{"disambiguationData":[OSD([sQuery(id+"F0.wireOp",EDGE,"E54.bottom"),sQuery(id+"F0.wireOp",EDGE,"E55.top"),sQuery(id+"F0.wireOp",EDGE,"E55.left")])]});
            fillet(context, id + "F3", {"entities" : qUnion([Q0, Q1, Q2, Q3, Q4, Q5, Q6, Q7, Q8, Q9, Q10, Q11, Q12, Q13, Q14, Q15, Q16, Q17, Q18, Q19]), "radius" : 1 * mm, "tangentPropagation" : true, "allowEdgeOverflow" : false});
        }
        {
            var Q0;
            Q0=makeQuery(id+"F1.opExtrude","SWEPT_EDGE",EDGE,{"disambiguationData":[OSD([sQuery(id+"F0.wireOp",EDGE,"E2.bottom"),sQuery(id+"F0.wireOp",EDGE,"E20")])]});
            var Q1;
            Q1=makeQuery(id+"F1.opExtrude","SWEPT_EDGE",EDGE,{"disambiguationData":[OSD([sQuery(id+"F0.wireOp",EDGE,"E2.left"),sQuery(id+"F0.wireOp",EDGE,"E27")])]});
            var Q2;
            Q2=makeQuery(id+"F1.opExtrude","SWEPT_EDGE",EDGE,{"disambiguationData":[OSD([sQuery(id+"F0.wireOp",EDGE,"E2.top"),sQuery(id+"F0.wireOp",EDGE,"E25")])]});
            var Q3;
            Q3=makeQuery(id+"F1.opExtrude","SWEPT_EDGE",EDGE,{"disambiguationData":[OSD([sQuery(id+"F0.wireOp",EDGE,"E2.left"),sQuery(id+"F0.wireOp",EDGE,"E26")])]});
            var Q4;
            Q4=makeQuery(id+"F1.opExtrude","SWEPT_EDGE",EDGE,{"disambiguationData":[OSD([sQuery(id+"F0.wireOp",EDGE,"E2.top"),sQuery(id+"F0.wireOp",EDGE,"E24")])]});
            var Q5;
            Q5=makeQuery(id+"F1.opExtrude","SWEPT_EDGE",EDGE,{"disambiguationData":[OSD([sQuery(id+"F0.wireOp",EDGE,"E2.right"),sQuery(id+"F0.wireOp",EDGE,"E23")])]});
            var Q6;
            Q6=makeQuery(id+"F1.opExtrude","SWEPT_EDGE",EDGE,{"disambiguationData":[OSD([sQuery(id+"F0.wireOp",EDGE,"E2.right"),sQuery(id+"F0.wireOp",EDGE,"E22")])]});
            var Q7;
            Q7=makeQuery(id+"F1.opExtrude","SWEPT_EDGE",EDGE,{"disambiguationData":[OSD([sQuery(id+"F0.wireOp",EDGE,"E2.bottom"),sQuery(id+"F0.wireOp",EDGE,"E21")])]});
            fillet(context, id + "F4", {"entities" : qUnion([Q0, Q1, Q2, Q3, Q4, Q5, Q6, Q7]), "radius" : 1 * mm, "tangentPropagation" : true, "allowEdgeOverflow" : false});
        }
    });
